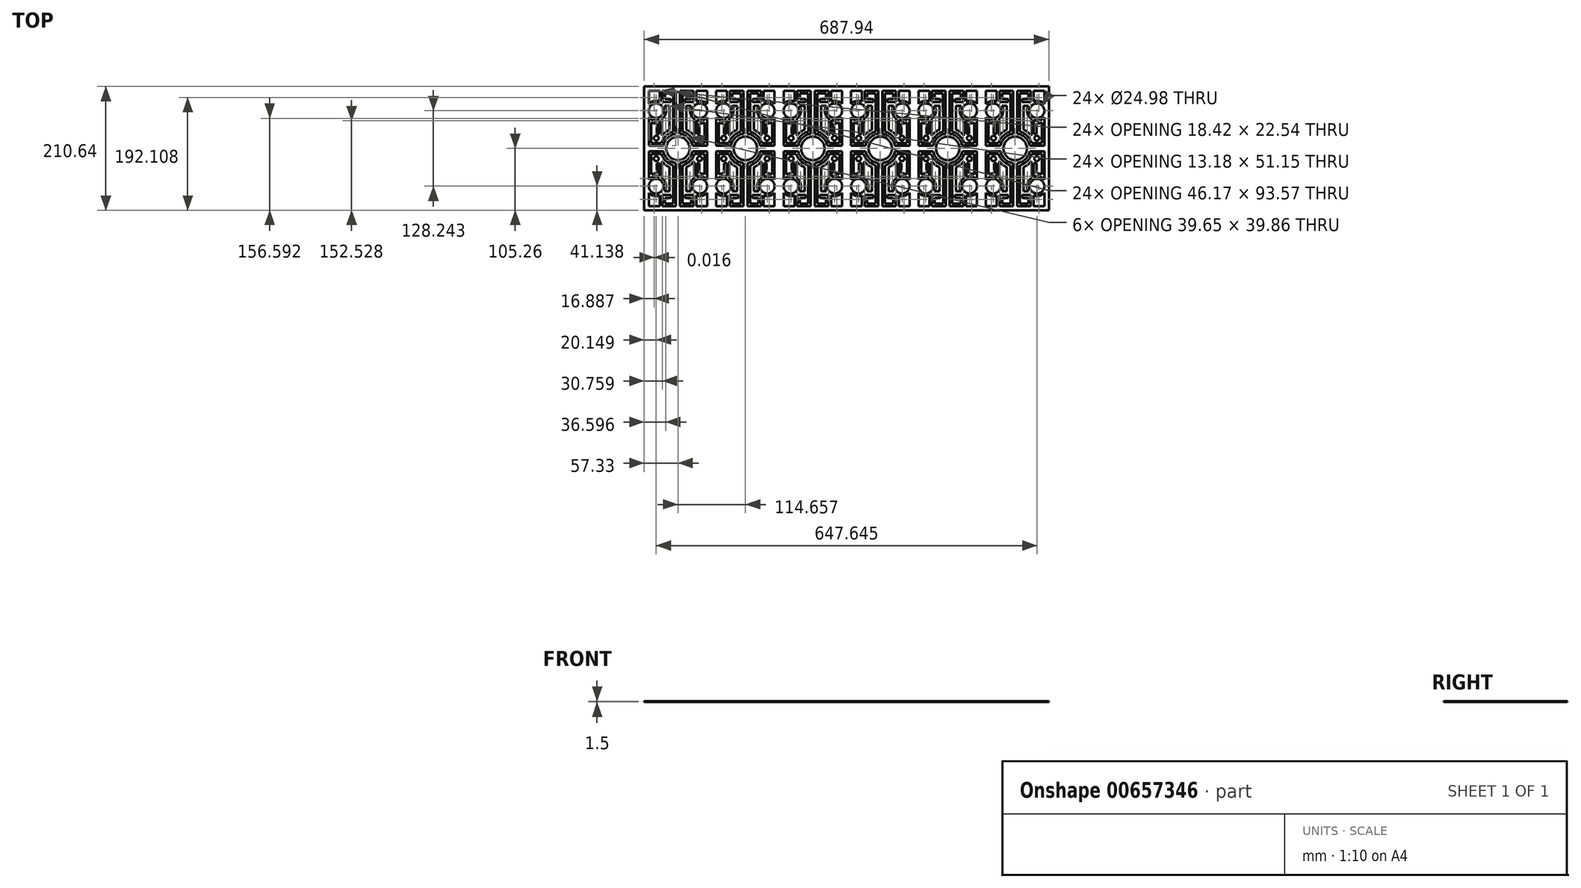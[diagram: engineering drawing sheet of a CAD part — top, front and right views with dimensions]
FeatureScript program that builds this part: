
annotation { "Feature Type Name" : "Feature", "Feature Type Description" : "" }
export const myFeature = defineFeature(function(context is Context, id is Id, definition is map)
    precondition{}
    {
        {
            var Q0;
            Q0=qCreatedBy(makeId("Top.planeOp"),FACE);
            var sketch = newSketch(context, id + "F0", { "sketchPlane" : qUnion([Q0])});
            skLineSegment(sketch, "E0.right", {"start": v(-57.33, -105.32) * mm, "end": v(-57.33, 105.32) * mm});
            skPoint(sketch, "E1.MirrorP", {"position": v(-114.66, 0) * mm});
            skLineSegment(sketch, "E2.MirrorCS", {"start": v(-137.32, -72.9) * mm, "end": v(-128.78, -72.9) * mm});
            skLineSegment(sketch, "E3.MirrorCS", {"start": v(-141.1, -98.18) * mm, "end": v(-141.1, -79.06) * mm});
            skLineSegment(sketch, "E4.MirrorCS", {"start": v(-136.9, 84.17) * mm, "end": v(-136.9, 93.38) * mm});
            skLineSegment(sketch, "E5.MirrorCS", {"start": v(-88.2, 98.06) * mm, "end": v(-88.2, 78.94) * mm});
            skLineSegment(sketch, "E6.MirrorCS", {"start": v(-83.03, 24.9) * mm, "end": v(-78.45, 24.9) * mm});
            skLineSegment(sketch, "E7.MirrorCS", {"start": v(-126.45, -79.06) * mm, "end": v(-126.45, -84.3) * mm});
            skLineSegment(sketch, "E8.MirrorCS", {"start": v(-136.89, -84.3) * mm, "end": v(-136.89, -93.5) * mm});
            skLineSegment(sketch, "E9.MirrorCS", {"start": v(-92.41, 84.17) * mm, "end": v(-92.41, 93.38) * mm});
            skLineSegment(sketch, "E10.MirrorCS", {"start": v(-141.1, 98.06) * mm, "end": v(-141.1, 78.94) * mm});
            skLineSegment(sketch, "E11.MirrorCS", {"start": v(-92.43, -84.3) * mm, "end": v(-92.43, -93.5) * mm});
            skLineSegment(sketch, "E12.MirrorCS", {"start": v(-83.04, -25.02) * mm, "end": v(-78.47, -25.02) * mm});
            skLineSegment(sketch, "E13.MirrorCS", {"start": v(-126.47, 78.94) * mm, "end": v(-126.47, 84.17) * mm});
            skLineSegment(sketch, "E14.MirrorCS", {"start": v(-146.29, 24.9) * mm, "end": v(-150.86, 24.9) * mm});
            skLineSegment(sketch, "E15.MirrorCS", {"start": v(-137.34, 72.78) * mm, "end": v(-128.8, 72.78) * mm});
            skLineSegment(sketch, "E16.MirrorCS", {"start": v(-92, -72.9) * mm, "end": v(-100.53, -72.9) * mm});
            skLineSegment(sketch, "E17.MirrorCS", {"start": v(-102.86, -79.06) * mm, "end": v(-102.86, -84.3) * mm});
            skArc(sketch, "E18.MirrorCS", {"start": v(-150.85, -42.56) * mm, "mid": v(-155.51, -42.86) * mm, "end": v(-160, -44.15) * mm});
            skArc(sketch, "E19.MirrorCS", {"start": v(-78.47, -42.56) * mm, "mid": v(-73.8, -42.86) * mm, "end": v(-69.3, -44.15) * mm});
            skArc(sketch, "E20.MirrorCS", {"start": v(-150.86, 42.44) * mm, "mid": v(-155.53, 42.74) * mm, "end": v(-160.03, 44.03) * mm});
            skArc(sketch, "E21.MirrorCS", {"start": v(-78.45, 42.44) * mm, "mid": v(-73.78, 42.74) * mm, "end": v(-69.29, 44.03) * mm});
            skLineSegment(sketch, "E22.MirrorCS", {"start": v(-91.98, 72.78) * mm, "end": v(-100.51, 72.78) * mm});
            skLineSegment(sketch, "E23.MirrorCS", {"start": v(-88.22, -98.18) * mm, "end": v(-88.22, -79.06) * mm});
            skLineSegment(sketch, "E24.MirrorCS", {"start": v(-146.27, -25.02) * mm, "end": v(-150.85, -25.02) * mm});
            skLineSegment(sketch, "E25.MirrorCS", {"start": v(-102.84, 78.94) * mm, "end": v(-102.84, 84.17) * mm});
            skCircle(sketch, "E26.MirrorC", {"center": v(-114.66, 0) * mm, "radius": 19.87 * mm});
            skPoint(sketch, "E27.MirrorP", {"position": v(-114.64, -0.12) * mm});
            skCircle(sketch, "E28.MirrorC", {"center": v(-114.64, -0.12) * mm, "radius": 19.87 * mm});
            skCircle(sketch, "E29.MirrorC", {"center": v(-151.48, -17.57) * mm, "radius": 4.15 * mm});
            skLineSegment(sketch, "E30.MirrorCS", {"start": v(-92.43, -93.5) * mm, "end": v(-106.74, -93.5) * mm});
            skLineSegment(sketch, "E31.MirrorCS", {"start": v(-102.86, -84.3) * mm, "end": v(-92.43, -84.3) * mm});
            skLineSegment(sketch, "E32.MirrorCS", {"start": v(-106.72, 93.38) * mm, "end": v(-106.82, 28.61) * mm});
            skLineSegment(sketch, "E33.MirrorCS", {"start": v(-164.31, 4.49) * mm, "end": v(-139.42, 4.49) * mm});
            skLineSegment(sketch, "E34.MirrorCS", {"start": v(-118.14, 98.06) * mm, "end": v(-141.1, 98.06) * mm});
            skLineSegment(sketch, "E35.MirrorCS", {"start": v(-118.13, -25.04) * mm, "end": v(-118.13, -98.18) * mm});
            skLineSegment(sketch, "E36.MirrorCS", {"start": v(-65, 4.49) * mm, "end": v(-89.9, 4.49) * mm});
            skLineSegment(sketch, "E37.MirrorCS", {"start": v(-164.3, -98.18) * mm, "end": v(-145.87, -98.18) * mm});
            skLineSegment(sketch, "E38.MirrorCS", {"start": v(-171.99, 105.32) * mm, "end": v(-57.33, 105.32) * mm});
            skLineSegment(sketch, "E39.MirrorCS", {"start": v(-83.44, -98.18) * mm, "end": v(-83.44, -80.04) * mm});
            skLineSegment(sketch, "E40.MirrorCS", {"start": v(-69.29, 9) * mm, "end": v(-86.39, 9) * mm});
            skLineSegment(sketch, "E41.MirrorCS", {"start": v(-100.53, -72.9) * mm, "end": v(-100.53, -31.97) * mm});
            skLineSegment(sketch, "E42.MirrorCS", {"start": v(-164.31, 98.06) * mm, "end": v(-145.89, 98.06) * mm});
            skArc(sketch, "E43.MirrorCS", {"start": v(-87.33, 21.63) * mm, "mid": v(-93.3, 27.54) * mm, "end": v(-100.51, 31.85) * mm});
            skLineSegment(sketch, "E44.MirrorCS", {"start": v(-128.8, 72.78) * mm, "end": v(-128.8, 31.85) * mm});
            skArc(sketch, "E45.MirrorCS", {"start": v(-141.97, -50.43) * mm, "mid": v(-135.25, -60.76) * mm, "end": v(-137.32, -72.9) * mm});
            skArc(sketch, "E46.MirrorCS", {"start": v(-65.02, -52.91) * mm, "mid": v(-73.34, -47.9) * mm, "end": v(-83.04, -48.31) * mm});
            skArc(sketch, "E47.MirrorCS", {"start": v(-65.02, -75.64) * mm, "mid": v(-73.56, -80.65) * mm, "end": v(-83.44, -80.04) * mm});
            skLineSegment(sketch, "E48.MirrorCS", {"start": v(-111.18, -25.04) * mm, "end": v(-111.18, -98.18) * mm});
            skCircle(sketch, "E49.MirrorC", {"center": v(-77.82, 17.45) * mm, "radius": 4.15 * mm});
            skLineSegment(sketch, "E50.MirrorCS", {"start": v(-145.89, 98.06) * mm, "end": v(-145.89, 79.92) * mm});
            skLineSegment(sketch, "E51.MirrorCS", {"start": v(-78.47, -25.02) * mm, "end": v(-78.47, -42.56) * mm});
            skLineSegment(sketch, "E52.MirrorCS", {"start": v(-136.89, -93.5) * mm, "end": v(-122.58, -93.5) * mm});
            skLineSegment(sketch, "E53.MirrorCS", {"start": v(-160, -44.15) * mm, "end": v(-160, -9.11) * mm});
            skArc(sketch, "E54.MirrorCS", {"start": v(-142.91, -9.11) * mm, "mid": v(-135.19, -21.52) * mm, "end": v(-122.47, -28.73) * mm});
            skLineSegment(sketch, "E55.MirrorCS", {"start": v(-150.85, -25.02) * mm, "end": v(-150.85, -42.56) * mm});
            skLineSegment(sketch, "E56.MirrorCS", {"start": v(-136.9, 93.38) * mm, "end": v(-122.6, 93.38) * mm});
            skLineSegment(sketch, "E57.MirrorCS", {"start": v(-102.84, 84.17) * mm, "end": v(-92.41, 84.17) * mm});
            skLineSegment(sketch, "E58.MirrorCS", {"start": v(-150.86, 24.9) * mm, "end": v(-150.86, 42.44) * mm});
            skCircle(sketch, "E59.MirrorC", {"center": v(-77.83, -17.57) * mm, "radius": 4.15 * mm});
            skLineSegment(sketch, "E60.MirrorCS", {"start": v(-100.51, 72.78) * mm, "end": v(-100.51, 31.85) * mm});
            skLineSegment(sketch, "E61.MirrorCS", {"start": v(-111.18, -98.18) * mm, "end": v(-88.22, -98.18) * mm});
            skLineSegment(sketch, "E62.MirrorCS", {"start": v(-160, -9.11) * mm, "end": v(-142.91, -9.11) * mm});
            skArc(sketch, "E63.MirrorCS", {"start": v(-164.3, -75.64) * mm, "mid": v(-155.76, -80.65) * mm, "end": v(-145.87, -80.04) * mm});
            skLineSegment(sketch, "E64.MirrorCS", {"start": v(-171.99, -105.32) * mm, "end": v(-57.33, -105.32) * mm});
            skPoint(sketch, "E65.MirrorP", {"position": v(-114.67, -0.12) * mm});
            skArc(sketch, "E66.MirrorCS", {"start": v(-65, 52.8) * mm, "mid": v(-73.32, 47.77) * mm, "end": v(-83.03, 48.2) * mm});
            skArc(sketch, "E67.MirrorCS", {"start": v(-89.9, 4.49) * mm, "mid": v(-97.22, 18.15) * mm, "end": v(-111.17, 24.92) * mm});
            skArc(sketch, "E68.MirrorCS", {"start": v(-87.35, -21.75) * mm, "mid": v(-93.32, -27.66) * mm, "end": v(-100.53, -31.97) * mm});
            skArc(sketch, "E69.MirrorCS", {"start": v(-86.4, -9.11) * mm, "mid": v(-94.13, -21.52) * mm, "end": v(-106.84, -28.73) * mm});
            skLineSegment(sketch, "E70.MirrorCS", {"start": v(-65.02, -98.18) * mm, "end": v(-65.02, -75.64) * mm});
            skLineSegment(sketch, "E71.MirrorCS", {"start": v(-164.3, -52.91) * mm, "end": v(-164.3, -4.6) * mm});
            skLineSegment(sketch, "E72.MirrorCS", {"start": v(-122.58, -93.5) * mm, "end": v(-122.47, -28.73) * mm});
            skLineSegment(sketch, "E73.MirrorCS", {"start": v(-69.3, -9.11) * mm, "end": v(-86.4, -9.11) * mm});
            skArc(sketch, "E74.MirrorCS", {"start": v(-164.31, 75.52) * mm, "mid": v(-155.77, 80.53) * mm, "end": v(-145.89, 79.92) * mm});
            skLineSegment(sketch, "E75.MirrorCS", {"start": v(-87.35, -50.43) * mm, "end": v(-87.35, -21.75) * mm});
            skLineSegment(sketch, "E76.MirrorCS", {"start": v(-141.1, 78.94) * mm, "end": v(-126.47, 78.94) * mm});
            skLineSegment(sketch, "E77.MirrorCS", {"start": v(-164.3, -98.18) * mm, "end": v(-164.3, -75.64) * mm});
            skLineSegment(sketch, "E78.MirrorCS", {"start": v(-65.02, -98.18) * mm, "end": v(-83.44, -98.18) * mm});
            skLineSegment(sketch, "E79.MirrorCS", {"start": v(-69.3, -44.15) * mm, "end": v(-69.3, -9.11) * mm});
            skLineSegment(sketch, "E80.MirrorCS", {"start": v(-146.27, -48.31) * mm, "end": v(-146.27, -25.02) * mm});
            skLineSegment(sketch, "E81.MirrorCS", {"start": v(-160.03, 9) * mm, "end": v(-142.93, 9) * mm});
            skLineSegment(sketch, "E82.MirrorCS", {"start": v(-141.97, -50.43) * mm, "end": v(-141.97, -21.75) * mm});
            skArc(sketch, "E83.MirrorCS", {"start": v(-87.33, 50.3) * mm, "mid": v(-94.05, 60.64) * mm, "end": v(-91.98, 72.78) * mm});
            skLineSegment(sketch, "E84.MirrorCS", {"start": v(-65.02, -52.91) * mm, "end": v(-65.02, -4.6) * mm});
            skLineSegment(sketch, "E85.MirrorCS", {"start": v(-164.31, 52.8) * mm, "end": v(-164.31, 4.49) * mm});
            skLineSegment(sketch, "E86.MirrorCS", {"start": v(-65, 98.06) * mm, "end": v(-83.43, 98.06) * mm});
            skCircle(sketch, "E87.MirrorC", {"center": v(-77.48, 64.06) * mm, "radius": 12.5 * mm});
            skLineSegment(sketch, "E88.MirrorCS", {"start": v(-78.45, 24.9) * mm, "end": v(-78.45, 42.44) * mm});
            skLineSegment(sketch, "E89.MirrorCS", {"start": v(-83.03, 48.2) * mm, "end": v(-83.03, 24.9) * mm});
            skLineSegment(sketch, "E90.MirrorCS", {"start": v(-171.99, -105.32) * mm, "end": v(-171.99, 105.32) * mm});
            skArc(sketch, "E91.MirrorCS", {"start": v(-65, 75.52) * mm, "mid": v(-73.54, 80.53) * mm, "end": v(-83.43, 79.92) * mm});
            skLineSegment(sketch, "E92.MirrorCS", {"start": v(-65, 52.8) * mm, "end": v(-65, 4.49) * mm});
            skArc(sketch, "E93.MirrorCS", {"start": v(-139.4, -4.6) * mm, "mid": v(-132.07, -18.27) * mm, "end": v(-118.13, -25.04) * mm});
            skLineSegment(sketch, "E94.MirrorCS", {"start": v(-83.04, -48.31) * mm, "end": v(-83.04, -25.02) * mm});
            skLineSegment(sketch, "E95.MirrorCS", {"start": v(-164.3, -4.6) * mm, "end": v(-139.4, -4.6) * mm});
            skLineSegment(sketch, "E96.MirrorCS", {"start": v(-88.2, 78.94) * mm, "end": v(-102.84, 78.94) * mm});
            skCircle(sketch, "E97.MirrorC", {"center": v(-151.5, 17.45) * mm, "radius": 4.15 * mm});
            skArc(sketch, "E98.MirrorCS", {"start": v(-141.97, -21.75) * mm, "mid": v(-136, -27.66) * mm, "end": v(-128.78, -31.97) * mm});
            skLineSegment(sketch, "E99.MirrorCS", {"start": v(-69.29, 44.03) * mm, "end": v(-69.29, 9) * mm});
            skArc(sketch, "E100.MirrorCS", {"start": v(-139.42, 4.49) * mm, "mid": v(-132.1, 18.15) * mm, "end": v(-118.14, 24.92) * mm});
            skLineSegment(sketch, "E101.MirrorCS", {"start": v(-88.22, -79.06) * mm, "end": v(-102.86, -79.06) * mm});
            skLineSegment(sketch, "E102.MirrorCS", {"start": v(-164.31, 98.06) * mm, "end": v(-164.31, 75.52) * mm});
            skArc(sketch, "E103.MirrorCS", {"start": v(-164.31, 52.8) * mm, "mid": v(-156, 47.77) * mm, "end": v(-146.29, 48.2) * mm});
            skCircle(sketch, "E104.MirrorC", {"center": v(-77.5, -64.18) * mm, "radius": 12.5 * mm});
            skLineSegment(sketch, "E105.MirrorCS", {"start": v(-111.17, 24.92) * mm, "end": v(-111.17, 98.06) * mm});
            skLineSegment(sketch, "E106.MirrorCS", {"start": v(-118.14, 24.92) * mm, "end": v(-118.14, 98.06) * mm});
            skCircle(sketch, "E107.MirrorC", {"center": v(-151.84, 64.06) * mm, "radius": 12.5 * mm});
            skArc(sketch, "E108.MirrorCS", {"start": v(-141.98, 21.63) * mm, "mid": v(-136.01, 27.54) * mm, "end": v(-128.8, 31.85) * mm});
            skLineSegment(sketch, "E109.MirrorCS", {"start": v(-160.03, 44.03) * mm, "end": v(-160.03, 9) * mm});
            skLineSegment(sketch, "E110.MirrorCS", {"start": v(-92.41, 93.38) * mm, "end": v(-106.72, 93.38) * mm});
            skLineSegment(sketch, "E111.MirrorCS", {"start": v(-141.1, -79.06) * mm, "end": v(-126.45, -79.06) * mm});
            skLineSegment(sketch, "E112.MirrorCS", {"start": v(-87.33, 50.3) * mm, "end": v(-87.33, 21.63) * mm});
            skLineSegment(sketch, "E113.MirrorCS", {"start": v(-146.29, 48.2) * mm, "end": v(-146.29, 24.9) * mm});
            skArc(sketch, "E114.MirrorCS", {"start": v(-87.35, -50.43) * mm, "mid": v(-94.06, -60.76) * mm, "end": v(-92, -72.9) * mm});
            skArc(sketch, "E115.MirrorCS", {"start": v(-164.3, -52.91) * mm, "mid": v(-155.98, -47.9) * mm, "end": v(-146.27, -48.31) * mm});
            skLineSegment(sketch, "E116.MirrorCS", {"start": v(-126.45, -84.3) * mm, "end": v(-136.89, -84.3) * mm});
            skArc(sketch, "E117.MirrorCS", {"start": v(-141.98, 50.3) * mm, "mid": v(-135.27, 60.64) * mm, "end": v(-137.34, 72.78) * mm});
            skLineSegment(sketch, "E118.MirrorCS", {"start": v(-65, 98.06) * mm, "end": v(-65, 75.52) * mm});
            skLineSegment(sketch, "E119.MirrorCS", {"start": v(-122.6, 93.38) * mm, "end": v(-122.5, 28.61) * mm});
            skLineSegment(sketch, "E120.MirrorCS", {"start": v(-106.74, -93.5) * mm, "end": v(-106.84, -28.73) * mm});
            skLineSegment(sketch, "E121.MirrorCS", {"start": v(-65.02, -4.6) * mm, "end": v(-89.91, -4.6) * mm});
            skLineSegment(sketch, "E122.MirrorCS", {"start": v(-83.43, 98.06) * mm, "end": v(-83.43, 79.92) * mm});
            skLineSegment(sketch, "E123.MirrorCS", {"start": v(-126.47, 84.17) * mm, "end": v(-136.9, 84.17) * mm});
            skLineSegment(sketch, "E124.MirrorCS", {"start": v(-111.17, 98.06) * mm, "end": v(-88.2, 98.06) * mm});
            skCircle(sketch, "E125.MirrorC", {"center": v(-151.82, -64.18) * mm, "radius": 12.5 * mm});
            skArc(sketch, "E126.MirrorCS", {"start": v(-142.93, 9) * mm, "mid": v(-135.2, 21.4) * mm, "end": v(-122.5, 28.61) * mm});
            skLineSegment(sketch, "E127.MirrorCS", {"start": v(-128.78, -72.9) * mm, "end": v(-128.78, -31.97) * mm});
            skLineSegment(sketch, "E128.MirrorCS", {"start": v(-118.13, -98.18) * mm, "end": v(-141.1, -98.18) * mm});
            skCircle(sketch, "E129.MirrorC", {"center": v(-114.67, -0.12) * mm, "radius": 19.87 * mm});
            skArc(sketch, "E130.MirrorCS", {"start": v(-89.91, -4.6) * mm, "mid": v(-97.24, -18.27) * mm, "end": v(-111.18, -25.04) * mm});
            skArc(sketch, "E131.MirrorCS", {"start": v(-86.39, 9) * mm, "mid": v(-94.11, 21.4) * mm, "end": v(-106.82, 28.61) * mm});
            skLineSegment(sketch, "E132.MirrorCS", {"start": v(-145.87, -98.18) * mm, "end": v(-145.87, -80.04) * mm});
            skLineSegment(sketch, "E133.MirrorCS", {"start": v(-141.98, 50.3) * mm, "end": v(-141.98, 21.63) * mm});
            skPoint(sketch, "E134.MirrorP", {"position": v(0, 0) * mm});
            skArc(sketch, "E135.MirrorCS", {"start": v(36.2, 42.44) * mm, "mid": v(40.87, 42.74) * mm, "end": v(45.37, 44.03) * mm});
            skLineSegment(sketch, "E136.MirrorCS", {"start": v(22.66, -72.9) * mm, "end": v(14.13, -72.9) * mm});
            skLineSegment(sketch, "E137.MirrorCS", {"start": v(-22.66, -72.9) * mm, "end": v(-14.13, -72.9) * mm});
            skLineSegment(sketch, "E138.MirrorCS", {"start": v(22.68, 72.78) * mm, "end": v(14.14, 72.78) * mm});
            skLineSegment(sketch, "E139.MirrorCS", {"start": v(31.63, 24.9) * mm, "end": v(36.2, 24.9) * mm});
            skLineSegment(sketch, "E140.MirrorCS", {"start": v(-26.45, 78.94) * mm, "end": v(-11.81, 78.94) * mm});
            skLineSegment(sketch, "E141.MirrorCS", {"start": v(26.44, -79.06) * mm, "end": v(11.8, -79.06) * mm});
            skLineSegment(sketch, "E142.MirrorCS", {"start": v(-11.8, -84.3) * mm, "end": v(-22.23, -84.3) * mm});
            skLineSegment(sketch, "E143.MirrorCS", {"start": v(-11.81, 84.17) * mm, "end": v(-22.25, 84.17) * mm});
            skLineSegment(sketch, "E144.MirrorCS", {"start": v(31.62, -25.02) * mm, "end": v(36.19, -25.02) * mm});
            skLineSegment(sketch, "E145.MirrorCS", {"start": v(26.44, -98.18) * mm, "end": v(26.44, -79.06) * mm});
            skLineSegment(sketch, "E146.MirrorCS", {"start": v(22.25, 84.17) * mm, "end": v(22.25, 93.38) * mm});
            skLineSegment(sketch, "E147.MirrorCS", {"start": v(-26.45, 98.06) * mm, "end": v(-26.45, 78.94) * mm});
            skLineSegment(sketch, "E148.MirrorCS", {"start": v(-26.44, -98.18) * mm, "end": v(-26.44, -79.06) * mm});
            skLineSegment(sketch, "E149.MirrorCS", {"start": v(11.81, 84.17) * mm, "end": v(22.25, 84.17) * mm});
            skLineSegment(sketch, "E150.MirrorCS", {"start": v(-31.63, 24.9) * mm, "end": v(-36.2, 24.9) * mm});
            skLineSegment(sketch, "E151.MirrorCS", {"start": v(-26.44, -79.06) * mm, "end": v(-11.8, -79.06) * mm});
            skLineSegment(sketch, "E152.MirrorCS", {"start": v(11.8, -84.3) * mm, "end": v(22.23, -84.3) * mm});
            skArc(sketch, "E153.MirrorCS", {"start": v(-36.2, 42.44) * mm, "mid": v(-40.87, 42.74) * mm, "end": v(-45.37, 44.03) * mm});
            skLineSegment(sketch, "E154.MirrorCS", {"start": v(11.8, -79.06) * mm, "end": v(11.8, -84.3) * mm});
            skLineSegment(sketch, "E155.MirrorCS", {"start": v(22.23, -84.3) * mm, "end": v(22.23, -93.5) * mm});
            skLineSegment(sketch, "E156.MirrorCS", {"start": v(-22.25, 84.17) * mm, "end": v(-22.25, 93.38) * mm});
            skLineSegment(sketch, "E157.MirrorCS", {"start": v(26.45, 98.06) * mm, "end": v(26.45, 78.94) * mm});
            skLineSegment(sketch, "E158.MirrorCS", {"start": v(-22.23, -84.3) * mm, "end": v(-22.23, -93.5) * mm});
            skLineSegment(sketch, "E159.MirrorCS", {"start": v(-31.62, -25.02) * mm, "end": v(-36.19, -25.02) * mm});
            skArc(sketch, "E160.MirrorCS", {"start": v(49.65, 52.8) * mm, "mid": v(41.34, 47.77) * mm, "end": v(31.63, 48.2) * mm});
            skArc(sketch, "E161.MirrorCS", {"start": v(36.19, -42.56) * mm, "mid": v(40.86, -42.86) * mm, "end": v(45.35, -44.15) * mm});
            skLineSegment(sketch, "E162.MirrorCS", {"start": v(26.45, 78.94) * mm, "end": v(11.81, 78.94) * mm});
            skLineSegment(sketch, "E163.MirrorCS", {"start": v(-11.8, -79.06) * mm, "end": v(-11.8, -84.3) * mm});
            skLineSegment(sketch, "E164.MirrorCS", {"start": v(-22.68, 72.78) * mm, "end": v(-14.14, 72.78) * mm});
            skArc(sketch, "E165.MirrorCS", {"start": v(-27.33, 21.63) * mm, "mid": v(-21.35, 27.54) * mm, "end": v(-14.14, 31.85) * mm});
            skArc(sketch, "E166.MirrorCS", {"start": v(-36.19, -42.56) * mm, "mid": v(-40.86, -42.86) * mm, "end": v(-45.35, -44.15) * mm});
            skLineSegment(sketch, "E167.MirrorCS", {"start": v(11.81, 78.94) * mm, "end": v(11.81, 84.17) * mm});
            skLineSegment(sketch, "E168.MirrorCS", {"start": v(-11.81, 78.94) * mm, "end": v(-11.81, 84.17) * mm});
            skCircle(sketch, "E169.MirrorC", {"center": v(0, 0) * mm, "radius": 19.87 * mm});
            skCircle(sketch, "E170.MirrorC", {"center": v(36.84, 17.45) * mm, "radius": 4.15 * mm});
            skCircle(sketch, "E171.MirrorC", {"center": v(-0.02, -0.12) * mm, "radius": 19.87 * mm});
            skCircle(sketch, "E172.MirrorC", {"center": v(-36.83, -17.57) * mm, "radius": 4.15 * mm});
            skPoint(sketch, "E173.MirrorP", {"position": v(0.02, -0.12) * mm});
            skCircle(sketch, "E174.MirrorC", {"center": v(-36.84, 17.45) * mm, "radius": 4.15 * mm});
            skCircle(sketch, "E175.MirrorC", {"center": v(36.83, -17.57) * mm, "radius": 4.15 * mm});
            skLineSegment(sketch, "E176.MirrorCS", {"start": v(49.64, -98.18) * mm, "end": v(49.64, -75.64) * mm});
            skLineSegment(sketch, "E177.MirrorCS", {"start": v(45.37, 9) * mm, "end": v(28.27, 9) * mm});
            skLineSegment(sketch, "E178.MirrorCS", {"start": v(-49.65, 98.06) * mm, "end": v(-31.23, 98.06) * mm});
            skLineSegment(sketch, "E179.MirrorCS", {"start": v(-49.64, -98.18) * mm, "end": v(-49.64, -75.64) * mm});
            skLineSegment(sketch, "E180.MirrorCS", {"start": v(45.35, -44.15) * mm, "end": v(45.35, -9.11) * mm});
            skLineSegment(sketch, "E181.MirrorCS", {"start": v(49.64, -98.18) * mm, "end": v(31.21, -98.18) * mm});
            skLineSegment(sketch, "E182.MirrorCS", {"start": v(27.33, 50.3) * mm, "end": v(27.33, 21.63) * mm});
            skArc(sketch, "E183.MirrorCS", {"start": v(27.33, 50.3) * mm, "mid": v(20.61, 60.64) * mm, "end": v(22.68, 72.78) * mm});
            skLineSegment(sketch, "E184.MirrorCS", {"start": v(49.65, 98.06) * mm, "end": v(49.65, 75.52) * mm});
            skLineSegment(sketch, "E185.MirrorCS", {"start": v(57.33, -105.32) * mm, "end": v(-57.33, -105.32) * mm});
            skLineSegment(sketch, "E186.MirrorCS", {"start": v(14.13, -72.9) * mm, "end": v(14.13, -31.97) * mm});
            skArc(sketch, "E187.MirrorCS", {"start": v(49.64, -75.64) * mm, "mid": v(41.1, -80.65) * mm, "end": v(31.21, -80.04) * mm});
            skArc(sketch, "E188.MirrorCS", {"start": v(-49.64, -75.64) * mm, "mid": v(-41.1, -80.65) * mm, "end": v(-31.21, -80.04) * mm});
            skLineSegment(sketch, "E189.MirrorCS", {"start": v(3.49, 24.92) * mm, "end": v(3.49, 98.06) * mm});
            skLineSegment(sketch, "E190.MirrorCS", {"start": v(-14.13, -72.9) * mm, "end": v(-14.13, -31.97) * mm});
            skLineSegment(sketch, "E191.MirrorCS", {"start": v(-49.64, -4.6) * mm, "end": v(-24.75, -4.6) * mm});
            skLineSegment(sketch, "E192.MirrorCS", {"start": v(-3.49, 24.92) * mm, "end": v(-3.49, 98.06) * mm});
            skLineSegment(sketch, "E193.MirrorCS", {"start": v(-7.92, -93.5) * mm, "end": v(-7.82, -28.73) * mm});
            skLineSegment(sketch, "E194.MirrorCS", {"start": v(-45.37, 9) * mm, "end": v(-28.27, 9) * mm});
            skLineSegment(sketch, "E195.MirrorCS", {"start": v(22.25, 93.38) * mm, "end": v(7.94, 93.38) * mm});
            skLineSegment(sketch, "E196.MirrorCS", {"start": v(-31.63, 48.2) * mm, "end": v(-31.63, 24.9) * mm});
            skLineSegment(sketch, "E197.MirrorCS", {"start": v(-45.35, -9.11) * mm, "end": v(-28.25, -9.11) * mm});
            skLineSegment(sketch, "E198.MirrorCS", {"start": v(57.33, -105.32) * mm, "end": v(57.33, 105.32) * mm});
            skArc(sketch, "E199.MirrorCS", {"start": v(49.65, 75.52) * mm, "mid": v(41.12, 80.53) * mm, "end": v(31.23, 79.92) * mm});
            skLineSegment(sketch, "E200.MirrorCS", {"start": v(-3.47, -25.04) * mm, "end": v(-3.47, -98.18) * mm});
            skLineSegment(sketch, "E201.MirrorCS", {"start": v(3.47, -98.18) * mm, "end": v(26.44, -98.18) * mm});
            skLineSegment(sketch, "E202.MirrorCS", {"start": v(-7.94, 93.38) * mm, "end": v(-7.83, 28.61) * mm});
            skLineSegment(sketch, "E203.MirrorCS", {"start": v(-27.33, 50.3) * mm, "end": v(-27.33, 21.63) * mm});
            skArc(sketch, "E204.MirrorCS", {"start": v(24.75, -4.6) * mm, "mid": v(17.42, -18.27) * mm, "end": v(3.47, -25.04) * mm});
            skLineSegment(sketch, "E205.MirrorCS", {"start": v(31.62, -48.31) * mm, "end": v(31.62, -25.02) * mm});
            skLineSegment(sketch, "E206.MirrorCS", {"start": v(31.21, -98.18) * mm, "end": v(31.21, -80.04) * mm});
            skLineSegment(sketch, "E207.MirrorCS", {"start": v(-45.35, -44.15) * mm, "end": v(-45.35, -9.11) * mm});
            skLineSegment(sketch, "E208.MirrorCS", {"start": v(49.64, -4.6) * mm, "end": v(24.75, -4.6) * mm});
            skLineSegment(sketch, "E209.MirrorCS", {"start": v(-22.25, 93.38) * mm, "end": v(-7.94, 93.38) * mm});
            skArc(sketch, "E210.MirrorCS", {"start": v(28.27, 9) * mm, "mid": v(20.55, 21.4) * mm, "end": v(7.83, 28.61) * mm});
            skCircle(sketch, "E211.MirrorC", {"center": v(-37.18, 64.06) * mm, "radius": 12.5 * mm});
            skLineSegment(sketch, "E212.MirrorCS", {"start": v(49.64, -52.91) * mm, "end": v(49.64, -4.6) * mm});
            skLineSegment(sketch, "E213.MirrorCS", {"start": v(57.33, 105.32) * mm, "end": v(-57.33, 105.32) * mm});
            skArc(sketch, "E214.MirrorCS", {"start": v(28.25, -9.11) * mm, "mid": v(20.53, -21.52) * mm, "end": v(7.82, -28.73) * mm});
            skLineSegment(sketch, "E215.MirrorCS", {"start": v(-49.65, 4.49) * mm, "end": v(-24.76, 4.49) * mm});
            skLineSegment(sketch, "E216.MirrorCS", {"start": v(22.23, -93.5) * mm, "end": v(7.92, -93.5) * mm});
            skLineSegment(sketch, "E217.MirrorCS", {"start": v(-22.23, -93.5) * mm, "end": v(-7.92, -93.5) * mm});
            skLineSegment(sketch, "E218.MirrorCS", {"start": v(-49.65, 98.06) * mm, "end": v(-49.65, 75.52) * mm});
            skLineSegment(sketch, "E219.MirrorCS", {"start": v(-49.65, 52.8) * mm, "end": v(-49.65, 4.49) * mm});
            skLineSegment(sketch, "E220.MirrorCS", {"start": v(-49.64, -52.91) * mm, "end": v(-49.64, -4.6) * mm});
            skArc(sketch, "E221.MirrorCS", {"start": v(-27.3, -21.75) * mm, "mid": v(-21.34, -27.66) * mm, "end": v(-14.13, -31.97) * mm});
            skArc(sketch, "E222.MirrorCS", {"start": v(27.33, 21.63) * mm, "mid": v(21.35, 27.54) * mm, "end": v(14.14, 31.85) * mm});
            skLineSegment(sketch, "E223.MirrorCS", {"start": v(-14.14, 72.78) * mm, "end": v(-14.14, 31.85) * mm});
            skLineSegment(sketch, "E224.MirrorCS", {"start": v(14.14, 72.78) * mm, "end": v(14.14, 31.85) * mm});
            skLineSegment(sketch, "E225.MirrorCS", {"start": v(-3.49, 98.06) * mm, "end": v(-26.45, 98.06) * mm});
            skLineSegment(sketch, "E226.MirrorCS", {"start": v(31.23, 98.06) * mm, "end": v(31.23, 79.92) * mm});
            skLineSegment(sketch, "E227.MirrorCS", {"start": v(3.49, 98.06) * mm, "end": v(26.45, 98.06) * mm});
            skArc(sketch, "E228.MirrorCS", {"start": v(-24.76, 4.49) * mm, "mid": v(-17.43, 18.15) * mm, "end": v(-3.49, 24.92) * mm});
            skArc(sketch, "E229.MirrorCS", {"start": v(-27.33, 50.3) * mm, "mid": v(-20.61, 60.64) * mm, "end": v(-22.68, 72.78) * mm});
            skLineSegment(sketch, "E230.MirrorCS", {"start": v(-36.19, -25.02) * mm, "end": v(-36.19, -42.56) * mm});
            skLineSegment(sketch, "E231.MirrorCS", {"start": v(3.47, -25.04) * mm, "end": v(3.47, -98.18) * mm});
            skArc(sketch, "E232.MirrorCS", {"start": v(-28.27, 9) * mm, "mid": v(-20.55, 21.4) * mm, "end": v(-7.83, 28.61) * mm});
            skArc(sketch, "E233.MirrorCS", {"start": v(49.64, -52.91) * mm, "mid": v(41.32, -47.9) * mm, "end": v(31.62, -48.31) * mm});
            skArc(sketch, "E234.MirrorCS", {"start": v(24.76, 4.49) * mm, "mid": v(17.43, 18.15) * mm, "end": v(3.49, 24.92) * mm});
            skLineSegment(sketch, "E235.MirrorCS", {"start": v(-45.37, 44.03) * mm, "end": v(-45.37, 9) * mm});
            skArc(sketch, "E236.MirrorCS", {"start": v(-27.3, -50.43) * mm, "mid": v(-20.6, -60.76) * mm, "end": v(-22.66, -72.9) * mm});
            skArc(sketch, "E237.MirrorCS", {"start": v(-24.75, -4.6) * mm, "mid": v(-17.42, -18.27) * mm, "end": v(-3.47, -25.04) * mm});
            skLineSegment(sketch, "E238.MirrorCS", {"start": v(-3.47, -98.18) * mm, "end": v(-26.44, -98.18) * mm});
            skArc(sketch, "E239.MirrorCS", {"start": v(27.3, -50.43) * mm, "mid": v(20.6, -60.76) * mm, "end": v(22.66, -72.9) * mm});
            skLineSegment(sketch, "E240.MirrorCS", {"start": v(31.63, 48.2) * mm, "end": v(31.63, 24.9) * mm});
            skLineSegment(sketch, "E241.MirrorCS", {"start": v(-36.2, 24.9) * mm, "end": v(-36.2, 42.44) * mm});
            skLineSegment(sketch, "E242.MirrorCS", {"start": v(36.19, -25.02) * mm, "end": v(36.19, -42.56) * mm});
            skLineSegment(sketch, "E243.MirrorCS", {"start": v(7.92, -93.5) * mm, "end": v(7.82, -28.73) * mm});
            skLineSegment(sketch, "E244.MirrorCS", {"start": v(-31.21, -98.18) * mm, "end": v(-31.21, -80.04) * mm});
            skCircle(sketch, "E245.MirrorC", {"center": v(-37.16, -64.18) * mm, "radius": 12.5 * mm});
            skLineSegment(sketch, "E246.MirrorCS", {"start": v(-27.3, -50.43) * mm, "end": v(-27.3, -21.75) * mm});
            skLineSegment(sketch, "E247.MirrorCS", {"start": v(45.37, 44.03) * mm, "end": v(45.37, 9) * mm});
            skCircle(sketch, "E248.MirrorC", {"center": v(37.18, 64.06) * mm, "radius": 12.5 * mm});
            skLineSegment(sketch, "E249.MirrorCS", {"start": v(7.94, 93.38) * mm, "end": v(7.83, 28.61) * mm});
            skLineSegment(sketch, "E250.MirrorCS", {"start": v(49.65, 4.49) * mm, "end": v(24.76, 4.49) * mm});
            skArc(sketch, "E251.MirrorCS", {"start": v(-49.64, -52.91) * mm, "mid": v(-41.32, -47.9) * mm, "end": v(-31.62, -48.31) * mm});
            skLineSegment(sketch, "E252.MirrorCS", {"start": v(36.2, 24.9) * mm, "end": v(36.2, 42.44) * mm});
            skArc(sketch, "E253.MirrorCS", {"start": v(27.3, -21.75) * mm, "mid": v(21.34, -27.66) * mm, "end": v(14.13, -31.97) * mm});
            skCircle(sketch, "E254.MirrorC", {"center": v(37.16, -64.18) * mm, "radius": 12.5 * mm});
            skLineSegment(sketch, "E255.MirrorCS", {"start": v(27.3, -50.43) * mm, "end": v(27.3, -21.75) * mm});
            skCircle(sketch, "E256.MirrorC", {"center": v(0.02, -0.12) * mm, "radius": 19.87 * mm});
            skLineSegment(sketch, "E257.MirrorCS", {"start": v(45.35, -9.11) * mm, "end": v(28.25, -9.11) * mm});
            skLineSegment(sketch, "E258.MirrorCS", {"start": v(49.65, 52.8) * mm, "end": v(49.65, 4.49) * mm});
            skLineSegment(sketch, "E259.MirrorCS", {"start": v(-49.64, -98.18) * mm, "end": v(-31.21, -98.18) * mm});
            skLineSegment(sketch, "E260.MirrorCS", {"start": v(-31.23, 98.06) * mm, "end": v(-31.23, 79.92) * mm});
            skLineSegment(sketch, "E261.MirrorCS", {"start": v(-31.62, -48.31) * mm, "end": v(-31.62, -25.02) * mm});
            skLineSegment(sketch, "E262.MirrorCS", {"start": v(49.65, 98.06) * mm, "end": v(31.23, 98.06) * mm});
            skArc(sketch, "E263.MirrorCS", {"start": v(-49.65, 75.52) * mm, "mid": v(-41.12, 80.53) * mm, "end": v(-31.23, 79.92) * mm});
            skArc(sketch, "E264.MirrorCS", {"start": v(-49.65, 52.8) * mm, "mid": v(-41.34, 47.77) * mm, "end": v(-31.63, 48.2) * mm});
            skArc(sketch, "E265.MirrorCS", {"start": v(-28.25, -9.11) * mm, "mid": v(-20.53, -21.52) * mm, "end": v(-7.82, -28.73) * mm});
            skPoint(sketch, "E266.MirrorP", {"position": v(229.31, 0) * mm});
            skPoint(sketch, "E267.MirrorP", {"position": v(114.66, 0) * mm});
            skLineSegment(sketch, "E268.MirrorCS", {"start": v(260.93, -25.02) * mm, "end": v(265.5, -25.02) * mm});
            skLineSegment(sketch, "E269.MirrorCS", {"start": v(197.68, 24.9) * mm, "end": v(193.1, 24.9) * mm});
            skArc(sketch, "E270.MirrorCS", {"start": v(265.52, 42.44) * mm, "mid": v(270.19, 42.74) * mm, "end": v(274.68, 44.03) * mm});
            skLineSegment(sketch, "E271.MirrorCS", {"start": v(137.34, 72.78) * mm, "end": v(128.8, 72.78) * mm});
            skLineSegment(sketch, "E272.MirrorCS", {"start": v(126.45, -84.3) * mm, "end": v(136.89, -84.3) * mm});
            skLineSegment(sketch, "E273.MirrorCS", {"start": v(102.84, 78.94) * mm, "end": v(102.84, 84.17) * mm});
            skLineSegment(sketch, "E274.MirrorCS", {"start": v(206.65, -72.9) * mm, "end": v(215.19, -72.9) * mm});
            skPoint(sketch, "E275.MirrorP", {"position": v(229.3, -0.12) * mm});
            skArc(sketch, "E276.MirrorCS", {"start": v(179.68, -52.91) * mm, "mid": v(188, -47.9) * mm, "end": v(197.7, -48.31) * mm});
            skArc(sketch, "E277.MirrorCS", {"start": v(193.1, 42.44) * mm, "mid": v(188.44, 42.74) * mm, "end": v(183.94, 44.03) * mm});
            skLineSegment(sketch, "E278.MirrorCS", {"start": v(126.47, 84.17) * mm, "end": v(136.9, 84.17) * mm});
            skLineSegment(sketch, "E279.MirrorCS", {"start": v(146.29, 24.9) * mm, "end": v(150.86, 24.9) * mm});
            skArc(sketch, "E280.MirrorCS", {"start": v(164.3, -52.91) * mm, "mid": v(155.98, -47.9) * mm, "end": v(146.27, -48.31) * mm});
            skLineSegment(sketch, "E281.MirrorCS", {"start": v(251.54, -84.3) * mm, "end": v(251.54, -93.5) * mm});
            skLineSegment(sketch, "E282.MirrorCS", {"start": v(92.43, -84.3) * mm, "end": v(92.43, -93.5) * mm});
            skLineSegment(sketch, "E283.MirrorCS", {"start": v(126.45, -79.06) * mm, "end": v(126.45, -84.3) * mm});
            skLineSegment(sketch, "E284.MirrorCS", {"start": v(88.22, -79.06) * mm, "end": v(102.86, -79.06) * mm});
            skLineSegment(sketch, "E285.MirrorCS", {"start": v(241.13, 84.17) * mm, "end": v(251.56, 84.17) * mm});
            skLineSegment(sketch, "E286.MirrorCS", {"start": v(88.2, 98.06) * mm, "end": v(88.2, 78.94) * mm});
            skLineSegment(sketch, "E287.MirrorCS", {"start": v(137.32, -72.9) * mm, "end": v(128.78, -72.9) * mm});
            skLineSegment(sketch, "E288.MirrorCS", {"start": v(202.88, -98.18) * mm, "end": v(202.88, -79.06) * mm});
            skLineSegment(sketch, "E289.MirrorCS", {"start": v(141.1, -79.06) * mm, "end": v(126.45, -79.06) * mm});
            skArc(sketch, "E290.MirrorCS", {"start": v(193.12, -42.56) * mm, "mid": v(188.46, -42.86) * mm, "end": v(183.96, -44.15) * mm});
            skLineSegment(sketch, "E291.MirrorCS", {"start": v(255.76, 78.94) * mm, "end": v(241.13, 78.94) * mm});
            skPoint(sketch, "E292.MirrorP", {"position": v(114.67, -0.12) * mm});
            skLineSegment(sketch, "E293.MirrorCS", {"start": v(260.94, 24.9) * mm, "end": v(265.52, 24.9) * mm});
            skLineSegment(sketch, "E294.MirrorCS", {"start": v(251.56, 84.17) * mm, "end": v(251.56, 93.38) * mm});
            skLineSegment(sketch, "E295.MirrorCS", {"start": v(102.86, -84.3) * mm, "end": v(92.43, -84.3) * mm});
            skLineSegment(sketch, "E296.MirrorCS", {"start": v(141.1, 78.94) * mm, "end": v(126.47, 78.94) * mm});
            skLineSegment(sketch, "E297.MirrorCS", {"start": v(91.98, 72.78) * mm, "end": v(100.51, 72.78) * mm});
            skArc(sketch, "E298.MirrorCS", {"start": v(278.95, -52.91) * mm, "mid": v(270.63, -47.9) * mm, "end": v(260.93, -48.31) * mm});
            skLineSegment(sketch, "E299.MirrorCS", {"start": v(83.04, -25.02) * mm, "end": v(78.47, -25.02) * mm});
            skLineSegment(sketch, "E300.MirrorCS", {"start": v(217.52, -84.3) * mm, "end": v(207.08, -84.3) * mm});
            skLineSegment(sketch, "E301.MirrorCS", {"start": v(202.86, 78.94) * mm, "end": v(217.5, 78.94) * mm});
            skLineSegment(sketch, "E302.MirrorCS", {"start": v(252, 72.78) * mm, "end": v(243.46, 72.78) * mm});
            skLineSegment(sketch, "E303.MirrorCS", {"start": v(217.5, 84.17) * mm, "end": v(207.07, 84.17) * mm});
            skLineSegment(sketch, "E304.MirrorCS", {"start": v(255.75, -98.18) * mm, "end": v(255.75, -79.06) * mm});
            skArc(sketch, "E305.MirrorCS", {"start": v(265.5, -42.56) * mm, "mid": v(270.17, -42.86) * mm, "end": v(274.67, -44.15) * mm});
            skLineSegment(sketch, "E306.MirrorCS", {"start": v(88.2, 78.94) * mm, "end": v(102.84, 78.94) * mm});
            skLineSegment(sketch, "E307.MirrorCS", {"start": v(88.22, -98.18) * mm, "end": v(88.22, -79.06) * mm});
            skLineSegment(sketch, "E308.MirrorCS", {"start": v(202.88, -79.06) * mm, "end": v(217.52, -79.06) * mm});
            skLineSegment(sketch, "E309.MirrorCS", {"start": v(102.86, -79.06) * mm, "end": v(102.86, -84.3) * mm});
            skArc(sketch, "E310.MirrorCS", {"start": v(164.31, 52.8) * mm, "mid": v(156, 47.77) * mm, "end": v(146.29, 48.2) * mm});
            skLineSegment(sketch, "E311.MirrorCS", {"start": v(202.86, 98.06) * mm, "end": v(202.86, 78.94) * mm});
            skLineSegment(sketch, "E312.MirrorCS", {"start": v(217.52, -79.06) * mm, "end": v(217.52, -84.3) * mm});
            skLineSegment(sketch, "E313.MirrorCS", {"start": v(92, -72.9) * mm, "end": v(100.53, -72.9) * mm});
            skLineSegment(sketch, "E314.MirrorCS", {"start": v(255.75, -79.06) * mm, "end": v(241.11, -79.06) * mm});
            skArc(sketch, "E315.MirrorCS", {"start": v(78.45, 42.44) * mm, "mid": v(73.78, 42.74) * mm, "end": v(69.29, 44.03) * mm});
            skArc(sketch, "E316.MirrorCS", {"start": v(78.47, -42.56) * mm, "mid": v(73.8, -42.86) * mm, "end": v(69.3, -44.15) * mm});
            skLineSegment(sketch, "E317.MirrorCS", {"start": v(207.08, -84.3) * mm, "end": v(207.08, -93.5) * mm});
            skArc(sketch, "E318.MirrorCS", {"start": v(65.02, -52.91) * mm, "mid": v(73.34, -47.9) * mm, "end": v(83.04, -48.31) * mm});
            skLineSegment(sketch, "E319.MirrorCS", {"start": v(126.47, 78.94) * mm, "end": v(126.47, 84.17) * mm});
            skLineSegment(sketch, "E320.MirrorCS", {"start": v(241.13, 78.94) * mm, "end": v(241.13, 84.17) * mm});
            skLineSegment(sketch, "E321.MirrorCS", {"start": v(251.98, -72.9) * mm, "end": v(243.44, -72.9) * mm});
            skLineSegment(sketch, "E322.MirrorCS", {"start": v(206.63, 72.78) * mm, "end": v(215.17, 72.78) * mm});
            skLineSegment(sketch, "E323.MirrorCS", {"start": v(241.11, -84.3) * mm, "end": v(251.54, -84.3) * mm});
            skLineSegment(sketch, "E324.MirrorCS", {"start": v(217.5, 78.94) * mm, "end": v(217.5, 84.17) * mm});
            skLineSegment(sketch, "E325.MirrorCS", {"start": v(92.41, 84.17) * mm, "end": v(92.41, 93.38) * mm});
            skLineSegment(sketch, "E326.MirrorCS", {"start": v(136.9, 84.17) * mm, "end": v(136.9, 93.38) * mm});
            skLineSegment(sketch, "E327.MirrorCS", {"start": v(102.84, 84.17) * mm, "end": v(92.41, 84.17) * mm});
            skLineSegment(sketch, "E328.MirrorCS", {"start": v(207.07, 84.17) * mm, "end": v(207.07, 93.38) * mm});
            skLineSegment(sketch, "E329.MirrorCS", {"start": v(136.89, -84.3) * mm, "end": v(136.89, -93.5) * mm});
            skLineSegment(sketch, "E330.MirrorCS", {"start": v(197.7, -25.02) * mm, "end": v(193.12, -25.02) * mm});
            skLineSegment(sketch, "E331.MirrorCS", {"start": v(255.76, 98.06) * mm, "end": v(255.76, 78.94) * mm});
            skArc(sketch, "E332.MirrorCS", {"start": v(150.85, -42.56) * mm, "mid": v(155.51, -42.86) * mm, "end": v(160, -44.15) * mm});
            skArc(sketch, "E333.MirrorCS", {"start": v(150.86, 42.44) * mm, "mid": v(155.53, 42.74) * mm, "end": v(160.03, 44.03) * mm});
            skLineSegment(sketch, "E334.MirrorCS", {"start": v(241.11, -79.06) * mm, "end": v(241.11, -84.3) * mm});
            skLineSegment(sketch, "E335.MirrorCS", {"start": v(146.27, -25.02) * mm, "end": v(150.85, -25.02) * mm});
            skLineSegment(sketch, "E336.MirrorCS", {"start": v(83.03, 24.9) * mm, "end": v(78.45, 24.9) * mm});
            skPoint(sketch, "E337.MirrorP", {"position": v(114.64, -0.12) * mm});
            skCircle(sketch, "E338.MirrorC", {"center": v(229.33, -0.12) * mm, "radius": 19.87 * mm});
            skCircle(sketch, "E339.MirrorC", {"center": v(77.82, 17.45) * mm, "radius": 4.15 * mm});
            skCircle(sketch, "E340.MirrorC", {"center": v(151.48, -17.57) * mm, "radius": 4.15 * mm});
            skCircle(sketch, "E341.MirrorC", {"center": v(77.83, -17.57) * mm, "radius": 4.15 * mm});
            skCircle(sketch, "E342.MirrorC", {"center": v(114.66, 0) * mm, "radius": 19.87 * mm});
            skCircle(sketch, "E343.MirrorC", {"center": v(229.31, 0) * mm, "radius": 19.87 * mm});
            skCircle(sketch, "E344.MirrorC", {"center": v(151.5, 17.45) * mm, "radius": 4.15 * mm});
            skCircle(sketch, "E345.MirrorC", {"center": v(192.49, -17.57) * mm, "radius": 4.15 * mm});
            skCircle(sketch, "E346.MirrorC", {"center": v(266.14, -17.57) * mm, "radius": 4.15 * mm});
            skCircle(sketch, "E347.MirrorC", {"center": v(192.47, 17.45) * mm, "radius": 4.15 * mm});
            skCircle(sketch, "E348.MirrorC", {"center": v(266.15, 17.45) * mm, "radius": 4.15 * mm});
            skCircle(sketch, "E349.MirrorC", {"center": v(114.64, -0.12) * mm, "radius": 19.87 * mm});
            skLineSegment(sketch, "E350.MirrorCS", {"start": v(83.03, 48.2) * mm, "end": v(83.03, 24.9) * mm});
            skLineSegment(sketch, "E351.MirrorCS", {"start": v(179.68, -4.6) * mm, "end": v(204.57, -4.6) * mm});
            skLineSegment(sketch, "E352.MirrorCS", {"start": v(128.8, 72.78) * mm, "end": v(128.8, 31.85) * mm});
            skLineSegment(sketch, "E353.MirrorCS", {"start": v(215.19, -72.9) * mm, "end": v(215.19, -31.97) * mm});
            skLineSegment(sketch, "E354.MirrorCS", {"start": v(197.68, 48.2) * mm, "end": v(197.68, 24.9) * mm});
            skCircle(sketch, "E355.MirrorC", {"center": v(151.84, 64.06) * mm, "radius": 12.5 * mm});
            skArc(sketch, "E356.MirrorCS", {"start": v(201.06, -9.11) * mm, "mid": v(208.78, -21.52) * mm, "end": v(221.5, -28.73) * mm});
            skArc(sketch, "E357.MirrorCS", {"start": v(89.91, -4.6) * mm, "mid": v(97.24, -18.27) * mm, "end": v(111.18, -25.04) * mm});
            skLineSegment(sketch, "E358.MirrorCS", {"start": v(256.62, -50.43) * mm, "end": v(256.62, -21.75) * mm});
            skArc(sketch, "E359.MirrorCS", {"start": v(179.66, 75.52) * mm, "mid": v(188.2, 80.53) * mm, "end": v(198.08, 79.92) * mm});
            skArc(sketch, "E360.MirrorCS", {"start": v(204.57, -4.6) * mm, "mid": v(211.9, -18.27) * mm, "end": v(225.84, -25.04) * mm});
            skLineSegment(sketch, "E361.MirrorCS", {"start": v(160, -9.11) * mm, "end": v(142.91, -9.11) * mm});
            skLineSegment(sketch, "E362.MirrorCS", {"start": v(65.02, -98.18) * mm, "end": v(83.44, -98.18) * mm});
            skArc(sketch, "E363.MirrorCS", {"start": v(202, -50.43) * mm, "mid": v(208.72, -60.76) * mm, "end": v(206.65, -72.9) * mm});
            skArc(sketch, "E364.MirrorCS", {"start": v(164.31, 75.52) * mm, "mid": v(155.77, 80.53) * mm, "end": v(145.89, 79.92) * mm});
            skLineSegment(sketch, "E365.MirrorCS", {"start": v(251.54, -93.5) * mm, "end": v(237.23, -93.5) * mm});
            skLineSegment(sketch, "E366.MirrorCS", {"start": v(215.17, 72.78) * mm, "end": v(215.17, 31.85) * mm});
            skLineSegment(sketch, "E367.MirrorCS", {"start": v(198.1, -98.18) * mm, "end": v(198.1, -80.04) * mm});
            skLineSegment(sketch, "E368.MirrorCS", {"start": v(260.94, 48.2) * mm, "end": v(260.94, 24.9) * mm});
            skCircle(sketch, "E369.MirrorC", {"center": v(77.5, -64.18) * mm, "radius": 12.5 * mm});
            skLineSegment(sketch, "E370.MirrorCS", {"start": v(111.17, 98.06) * mm, "end": v(88.2, 98.06) * mm});
            skLineSegment(sketch, "E371.MirrorCS", {"start": v(160, -44.15) * mm, "end": v(160, -9.11) * mm});
            skLineSegment(sketch, "E372.MirrorCS", {"start": v(65.02, -98.18) * mm, "end": v(65.02, -75.64) * mm});
            skLineSegment(sketch, "E373.MirrorCS", {"start": v(111.18, -25.04) * mm, "end": v(111.18, -98.18) * mm});
            skLineSegment(sketch, "E374.MirrorCS", {"start": v(274.68, 44.03) * mm, "end": v(274.68, 9) * mm});
            skLineSegment(sketch, "E375.MirrorCS", {"start": v(274.67, -9.11) * mm, "end": v(257.57, -9.11) * mm});
            skArc(sketch, "E376.MirrorCS", {"start": v(87.35, -50.43) * mm, "mid": v(94.06, -60.76) * mm, "end": v(92, -72.9) * mm});
            skLineSegment(sketch, "E377.MirrorCS", {"start": v(278.95, -98.18) * mm, "end": v(260.53, -98.18) * mm});
            skLineSegment(sketch, "E378.MirrorCS", {"start": v(65, 98.06) * mm, "end": v(65, 75.52) * mm});
            skLineSegment(sketch, "E379.MirrorCS", {"start": v(183.94, 44.03) * mm, "end": v(183.94, 9) * mm});
            skLineSegment(sketch, "E380.MirrorCS", {"start": v(160.03, 44.03) * mm, "end": v(160.03, 9) * mm});
            skLineSegment(sketch, "E381.MirrorCS", {"start": v(141.1, -98.18) * mm, "end": v(141.1, -79.06) * mm});
            skLineSegment(sketch, "E382.MirrorCS", {"start": v(106.72, 93.38) * mm, "end": v(106.82, 28.61) * mm});
            skLineSegment(sketch, "E383.MirrorCS", {"start": v(65.02, -52.91) * mm, "end": v(65.02, -4.6) * mm});
            skLineSegment(sketch, "E384.MirrorCS", {"start": v(146.29, 48.2) * mm, "end": v(146.29, 24.9) * mm});
            skArc(sketch, "E385.MirrorCS", {"start": v(256.64, 21.63) * mm, "mid": v(250.67, 27.54) * mm, "end": v(243.46, 31.85) * mm});
            skLineSegment(sketch, "E386.MirrorCS", {"start": v(198.08, 98.06) * mm, "end": v(198.08, 79.92) * mm});
            skLineSegment(sketch, "E387.MirrorCS", {"start": v(83.44, -98.18) * mm, "end": v(83.44, -80.04) * mm});
            skLineSegment(sketch, "E388.MirrorCS", {"start": v(69.3, -44.15) * mm, "end": v(69.3, -9.11) * mm});
            skLineSegment(sketch, "E389.MirrorCS", {"start": v(183.96, -44.15) * mm, "end": v(183.96, -9.11) * mm});
            skArc(sketch, "E390.MirrorCS", {"start": v(141.98, 50.3) * mm, "mid": v(135.27, 60.64) * mm, "end": v(137.34, 72.78) * mm});
            skCircle(sketch, "E391.MirrorC", {"center": v(151.82, -64.18) * mm, "radius": 12.5 * mm});
            skArc(sketch, "E392.MirrorCS", {"start": v(139.4, -4.6) * mm, "mid": v(132.07, -18.27) * mm, "end": v(118.13, -25.04) * mm});
            skLineSegment(sketch, "E393.MirrorCS", {"start": v(145.87, -98.18) * mm, "end": v(145.87, -80.04) * mm});
            skArc(sketch, "E394.MirrorCS", {"start": v(87.35, -21.75) * mm, "mid": v(93.32, -27.66) * mm, "end": v(100.53, -31.97) * mm});
            skLineSegment(sketch, "E395.MirrorCS", {"start": v(179.66, 52.8) * mm, "end": v(179.66, 4.49) * mm});
            skArc(sketch, "E396.MirrorCS", {"start": v(139.42, 4.49) * mm, "mid": v(132.1, 18.15) * mm, "end": v(118.14, 24.92) * mm});
            skLineSegment(sketch, "E397.MirrorCS", {"start": v(106.74, -93.5) * mm, "end": v(106.84, -28.73) * mm});
            skLineSegment(sketch, "E398.MirrorCS", {"start": v(286.64, -105.32) * mm, "end": v(286.64, 105.32) * mm});
            skLineSegment(sketch, "E399.MirrorCS", {"start": v(225.83, 24.92) * mm, "end": v(225.83, 98.06) * mm});
            skLineSegment(sketch, "E400.MirrorCS", {"start": v(243.46, 72.78) * mm, "end": v(243.46, 31.85) * mm});
            skLineSegment(sketch, "E401.MirrorCS", {"start": v(118.13, -25.04) * mm, "end": v(118.13, -98.18) * mm});
            skLineSegment(sketch, "E402.MirrorCS", {"start": v(92.43, -93.5) * mm, "end": v(106.74, -93.5) * mm});
            skLineSegment(sketch, "E403.MirrorCS", {"start": v(179.66, 98.06) * mm, "end": v(179.66, 75.52) * mm});
            skArc(sketch, "E404.MirrorCS", {"start": v(257.57, -9.11) * mm, "mid": v(249.84, -21.52) * mm, "end": v(237.13, -28.73) * mm});
            skLineSegment(sketch, "E405.MirrorCS", {"start": v(69.3, -9.11) * mm, "end": v(86.4, -9.11) * mm});
            skLineSegment(sketch, "E406.MirrorCS", {"start": v(150.86, 24.9) * mm, "end": v(150.86, 42.44) * mm});
            skLineSegment(sketch, "E407.MirrorCS", {"start": v(146.27, -48.31) * mm, "end": v(146.27, -25.02) * mm});
            skLineSegment(sketch, "E408.MirrorCS", {"start": v(78.45, 24.9) * mm, "end": v(78.45, 42.44) * mm});
            skArc(sketch, "E409.MirrorCS", {"start": v(164.3, -75.64) * mm, "mid": v(155.76, -80.65) * mm, "end": v(145.87, -80.04) * mm});
            skLineSegment(sketch, "E410.MirrorCS", {"start": v(251.56, 93.38) * mm, "end": v(237.25, 93.38) * mm});
            skLineSegment(sketch, "E411.MirrorCS", {"start": v(183.96, -9.11) * mm, "end": v(201.06, -9.11) * mm});
            skLineSegment(sketch, "E412.MirrorCS", {"start": v(237.23, -93.5) * mm, "end": v(237.13, -28.73) * mm});
            skCircle(sketch, "E413.MirrorC", {"center": v(266.48, -64.18) * mm, "radius": 12.5 * mm});
            skLineSegment(sketch, "E414.MirrorCS", {"start": v(145.89, 98.06) * mm, "end": v(145.89, 79.92) * mm});
            skLineSegment(sketch, "E415.MirrorCS", {"start": v(201.99, 50.3) * mm, "end": v(201.99, 21.63) * mm});
            skLineSegment(sketch, "E416.MirrorCS", {"start": v(164.3, -98.18) * mm, "end": v(145.87, -98.18) * mm});
            skLineSegment(sketch, "E417.MirrorCS", {"start": v(278.97, 98.06) * mm, "end": v(260.54, 98.06) * mm});
            skLineSegment(sketch, "E418.MirrorCS", {"start": v(141.98, 50.3) * mm, "end": v(141.98, 21.63) * mm});
            skLineSegment(sketch, "E419.MirrorCS", {"start": v(183.94, 9) * mm, "end": v(201.04, 9) * mm});
            skLineSegment(sketch, "E420.MirrorCS", {"start": v(164.3, -4.6) * mm, "end": v(139.4, -4.6) * mm});
            skLineSegment(sketch, "E421.MirrorCS", {"start": v(274.68, 9) * mm, "end": v(257.58, 9) * mm});
            skLineSegment(sketch, "E422.MirrorCS", {"start": v(221.4, -93.5) * mm, "end": v(221.5, -28.73) * mm});
            skLineSegment(sketch, "E423.MirrorCS", {"start": v(232.8, 24.92) * mm, "end": v(232.8, 98.06) * mm});
            skLineSegment(sketch, "E424.MirrorCS", {"start": v(237.25, 93.38) * mm, "end": v(237.15, 28.61) * mm});
            skLineSegment(sketch, "E425.MirrorCS", {"start": v(286.64, -105.32) * mm, "end": v(171.99, -105.32) * mm});
            skLineSegment(sketch, "E426.MirrorCS", {"start": v(225.83, 98.06) * mm, "end": v(202.86, 98.06) * mm});
            skArc(sketch, "E427.MirrorCS", {"start": v(256.62, -21.75) * mm, "mid": v(250.65, -27.66) * mm, "end": v(243.44, -31.97) * mm});
            skLineSegment(sketch, "E428.MirrorCS", {"start": v(278.97, 52.8) * mm, "end": v(278.97, 4.49) * mm});
            skLineSegment(sketch, "E429.MirrorCS", {"start": v(232.79, -25.04) * mm, "end": v(232.79, -98.18) * mm});
            skArc(sketch, "E430.MirrorCS", {"start": v(141.97, -21.75) * mm, "mid": v(136, -27.66) * mm, "end": v(128.78, -31.97) * mm});
            skLineSegment(sketch, "E431.MirrorCS", {"start": v(193.12, -25.02) * mm, "end": v(193.12, -42.56) * mm});
            skCircle(sketch, "E432.MirrorC", {"center": v(77.48, 64.06) * mm, "radius": 12.5 * mm});
            skArc(sketch, "E433.MirrorCS", {"start": v(254.08, 4.49) * mm, "mid": v(246.75, 18.15) * mm, "end": v(232.8, 24.92) * mm});
            skArc(sketch, "E434.MirrorCS", {"start": v(65.02, -75.64) * mm, "mid": v(73.56, -80.65) * mm, "end": v(83.44, -80.04) * mm});
            skArc(sketch, "E435.MirrorCS", {"start": v(89.9, 4.49) * mm, "mid": v(97.22, 18.15) * mm, "end": v(111.17, 24.92) * mm});
            skLineSegment(sketch, "E436.MirrorCS", {"start": v(164.31, 52.8) * mm, "end": v(164.31, 4.49) * mm});
            skLineSegment(sketch, "E437.MirrorCS", {"start": v(141.97, -50.43) * mm, "end": v(141.97, -21.75) * mm});
            skLineSegment(sketch, "E438.MirrorCS", {"start": v(65, 98.06) * mm, "end": v(83.43, 98.06) * mm});
            skLineSegment(sketch, "E439.MirrorCS", {"start": v(87.35, -50.43) * mm, "end": v(87.35, -21.75) * mm});
            skArc(sketch, "E440.MirrorCS", {"start": v(278.97, 75.52) * mm, "mid": v(270.43, 80.53) * mm, "end": v(260.54, 79.92) * mm});
            skArc(sketch, "E441.MirrorCS", {"start": v(201.04, 9) * mm, "mid": v(208.77, 21.4) * mm, "end": v(221.48, 28.61) * mm});
            skArc(sketch, "E442.MirrorCS", {"start": v(179.66, 52.8) * mm, "mid": v(187.98, 47.77) * mm, "end": v(197.68, 48.2) * mm});
            skLineSegment(sketch, "E443.MirrorCS", {"start": v(243.44, -72.9) * mm, "end": v(243.44, -31.97) * mm});
            skLineSegment(sketch, "E444.MirrorCS", {"start": v(150.85, -25.02) * mm, "end": v(150.85, -42.56) * mm});
            skLineSegment(sketch, "E445.MirrorCS", {"start": v(164.31, 4.49) * mm, "end": v(139.42, 4.49) * mm});
            skLineSegment(sketch, "E446.MirrorCS", {"start": v(278.95, -98.18) * mm, "end": v(278.95, -75.64) * mm});
            skArc(sketch, "E447.MirrorCS", {"start": v(179.68, -75.64) * mm, "mid": v(188.21, -80.65) * mm, "end": v(198.1, -80.04) * mm});
            skArc(sketch, "E448.MirrorCS", {"start": v(278.95, -75.64) * mm, "mid": v(270.41, -80.65) * mm, "end": v(260.53, -80.04) * mm});
            skLineSegment(sketch, "E449.MirrorCS", {"start": v(260.93, -48.31) * mm, "end": v(260.93, -25.02) * mm});
            skLineSegment(sketch, "E450.MirrorCS", {"start": v(179.68, -98.18) * mm, "end": v(198.1, -98.18) * mm});
            skArc(sketch, "E451.MirrorCS", {"start": v(202, -21.75) * mm, "mid": v(207.98, -27.66) * mm, "end": v(215.19, -31.97) * mm});
            skLineSegment(sketch, "E452.MirrorCS", {"start": v(286.64, 105.32) * mm, "end": v(171.99, 105.32) * mm});
            skLineSegment(sketch, "E453.MirrorCS", {"start": v(100.51, 72.78) * mm, "end": v(100.51, 31.85) * mm});
            skLineSegment(sketch, "E454.MirrorCS", {"start": v(179.68, -52.91) * mm, "end": v(179.68, -4.6) * mm});
            skArc(sketch, "E455.MirrorCS", {"start": v(87.33, 21.63) * mm, "mid": v(93.3, 27.54) * mm, "end": v(100.51, 31.85) * mm});
            skArc(sketch, "E456.MirrorCS", {"start": v(257.58, 9) * mm, "mid": v(249.86, 21.4) * mm, "end": v(237.15, 28.61) * mm});
            skCircle(sketch, "E457.MirrorC", {"center": v(229.3, -0.12) * mm, "radius": 19.87 * mm});
            skLineSegment(sketch, "E458.MirrorCS", {"start": v(278.95, -4.6) * mm, "end": v(254.06, -4.6) * mm});
            skArc(sketch, "E459.MirrorCS", {"start": v(141.97, -50.43) * mm, "mid": v(135.25, -60.76) * mm, "end": v(137.32, -72.9) * mm});
            skLineSegment(sketch, "E460.MirrorCS", {"start": v(164.3, -98.18) * mm, "end": v(164.3, -75.64) * mm});
            skLineSegment(sketch, "E461.MirrorCS", {"start": v(92.41, 93.38) * mm, "end": v(106.72, 93.38) * mm});
            skLineSegment(sketch, "E462.MirrorCS", {"start": v(225.84, -98.18) * mm, "end": v(202.88, -98.18) * mm});
            skLineSegment(sketch, "E463.MirrorCS", {"start": v(202, -50.43) * mm, "end": v(202, -21.75) * mm});
            skLineSegment(sketch, "E464.MirrorCS", {"start": v(265.5, -25.02) * mm, "end": v(265.5, -42.56) * mm});
            skLineSegment(sketch, "E465.MirrorCS", {"start": v(57.33, -105.32) * mm, "end": v(171.99, -105.32) * mm});
            skArc(sketch, "E466.MirrorCS", {"start": v(142.93, 9) * mm, "mid": v(135.2, 21.4) * mm, "end": v(122.5, 28.61) * mm});
            skLineSegment(sketch, "E467.MirrorCS", {"start": v(65, 4.49) * mm, "end": v(89.9, 4.49) * mm});
            skLineSegment(sketch, "E468.MirrorCS", {"start": v(278.97, 98.06) * mm, "end": v(278.97, 75.52) * mm});
            skLineSegment(sketch, "E469.MirrorCS", {"start": v(136.9, 93.38) * mm, "end": v(122.6, 93.38) * mm});
            skArc(sketch, "E470.MirrorCS", {"start": v(256.64, 50.3) * mm, "mid": v(249.92, 60.64) * mm, "end": v(252, 72.78) * mm});
            skArc(sketch, "E471.MirrorCS", {"start": v(86.4, -9.11) * mm, "mid": v(94.13, -21.52) * mm, "end": v(106.84, -28.73) * mm});
            skLineSegment(sketch, "E472.MirrorCS", {"start": v(57.33, 105.32) * mm, "end": v(171.99, 105.32) * mm});
            skCircle(sketch, "E473.MirrorC", {"center": v(192.15, -64.18) * mm, "radius": 12.5 * mm});
            skArc(sketch, "E474.MirrorCS", {"start": v(278.97, 52.8) * mm, "mid": v(270.65, 47.77) * mm, "end": v(260.94, 48.2) * mm});
            skArc(sketch, "E475.MirrorCS", {"start": v(65, 75.52) * mm, "mid": v(73.54, 80.53) * mm, "end": v(83.43, 79.92) * mm});
            skLineSegment(sketch, "E476.MirrorCS", {"start": v(136.89, -93.5) * mm, "end": v(122.58, -93.5) * mm});
            skLineSegment(sketch, "E477.MirrorCS", {"start": v(65.02, -4.6) * mm, "end": v(89.91, -4.6) * mm});
            skLineSegment(sketch, "E478.MirrorCS", {"start": v(69.29, 44.03) * mm, "end": v(69.29, 9) * mm});
            skLineSegment(sketch, "E479.MirrorCS", {"start": v(69.29, 9) * mm, "end": v(86.39, 9) * mm});
            skLineSegment(sketch, "E480.MirrorCS", {"start": v(256.64, 50.3) * mm, "end": v(256.64, 21.63) * mm});
            skLineSegment(sketch, "E481.MirrorCS", {"start": v(122.58, -93.5) * mm, "end": v(122.47, -28.73) * mm});
            skLineSegment(sketch, "E482.MirrorCS", {"start": v(221.38, 93.38) * mm, "end": v(221.48, 28.61) * mm});
            skLineSegment(sketch, "E483.MirrorCS", {"start": v(164.3, -52.91) * mm, "end": v(164.3, -4.6) * mm});
            skLineSegment(sketch, "E484.MirrorCS", {"start": v(87.33, 50.3) * mm, "end": v(87.33, 21.63) * mm});
            skLineSegment(sketch, "E485.MirrorCS", {"start": v(225.84, -25.04) * mm, "end": v(225.84, -98.18) * mm});
            skArc(sketch, "E486.MirrorCS", {"start": v(141.98, 21.63) * mm, "mid": v(136.01, 27.54) * mm, "end": v(128.8, 31.85) * mm});
            skLineSegment(sketch, "E487.MirrorCS", {"start": v(118.13, -98.18) * mm, "end": v(141.1, -98.18) * mm});
            skArc(sketch, "E488.MirrorCS", {"start": v(65, 52.8) * mm, "mid": v(73.32, 47.77) * mm, "end": v(83.03, 48.2) * mm});
            skLineSegment(sketch, "E489.MirrorCS", {"start": v(274.67, -44.15) * mm, "end": v(274.67, -9.11) * mm});
            skLineSegment(sketch, "E490.MirrorCS", {"start": v(160.03, 9) * mm, "end": v(142.93, 9) * mm});
            skLineSegment(sketch, "E491.MirrorCS", {"start": v(141.1, 98.06) * mm, "end": v(141.1, 78.94) * mm});
            skLineSegment(sketch, "E492.MirrorCS", {"start": v(179.68, -98.18) * mm, "end": v(179.68, -75.64) * mm});
            skLineSegment(sketch, "E493.MirrorCS", {"start": v(83.04, -48.31) * mm, "end": v(83.04, -25.02) * mm});
            skLineSegment(sketch, "E494.MirrorCS", {"start": v(207.07, 93.38) * mm, "end": v(221.38, 93.38) * mm});
            skCircle(sketch, "E495.MirrorC", {"center": v(114.67, -0.12) * mm, "radius": 19.87 * mm});
            skLineSegment(sketch, "E496.MirrorCS", {"start": v(278.95, -52.91) * mm, "end": v(278.95, -4.6) * mm});
            skArc(sketch, "E497.MirrorCS", {"start": v(201.99, 21.63) * mm, "mid": v(207.96, 27.54) * mm, "end": v(215.17, 31.85) * mm});
            skArc(sketch, "E498.MirrorCS", {"start": v(204.55, 4.49) * mm, "mid": v(211.88, 18.15) * mm, "end": v(225.83, 24.92) * mm});
            skLineSegment(sketch, "E499.MirrorCS", {"start": v(265.52, 24.9) * mm, "end": v(265.52, 42.44) * mm});
            skArc(sketch, "E500.MirrorCS", {"start": v(201.99, 50.3) * mm, "mid": v(208.7, 60.64) * mm, "end": v(206.63, 72.78) * mm});
            skLineSegment(sketch, "E501.MirrorCS", {"start": v(260.54, 98.06) * mm, "end": v(260.54, 79.92) * mm});
            skArc(sketch, "E502.MirrorCS", {"start": v(87.33, 50.3) * mm, "mid": v(94.05, 60.64) * mm, "end": v(91.98, 72.78) * mm});
            skLineSegment(sketch, "E503.MirrorCS", {"start": v(207.08, -93.5) * mm, "end": v(221.4, -93.5) * mm});
            skLineSegment(sketch, "E504.MirrorCS", {"start": v(197.7, -48.31) * mm, "end": v(197.7, -25.02) * mm});
            skLineSegment(sketch, "E505.MirrorCS", {"start": v(118.14, 24.92) * mm, "end": v(118.14, 98.06) * mm});
            skLineSegment(sketch, "E506.MirrorCS", {"start": v(111.18, -98.18) * mm, "end": v(88.22, -98.18) * mm});
            skLineSegment(sketch, "E507.MirrorCS", {"start": v(260.53, -98.18) * mm, "end": v(260.53, -80.04) * mm});
            skLineSegment(sketch, "E508.MirrorCS", {"start": v(78.47, -25.02) * mm, "end": v(78.47, -42.56) * mm});
            skLineSegment(sketch, "E509.MirrorCS", {"start": v(111.17, 24.92) * mm, "end": v(111.17, 98.06) * mm});
            skArc(sketch, "E510.MirrorCS", {"start": v(256.62, -50.43) * mm, "mid": v(249.9, -60.76) * mm, "end": v(251.98, -72.9) * mm});
            skLineSegment(sketch, "E511.MirrorCS", {"start": v(118.14, 98.06) * mm, "end": v(141.1, 98.06) * mm});
            skLineSegment(sketch, "E512.MirrorCS", {"start": v(164.31, 98.06) * mm, "end": v(145.89, 98.06) * mm});
            skLineSegment(sketch, "E513.MirrorCS", {"start": v(65, 52.8) * mm, "end": v(65, 4.49) * mm});
            skArc(sketch, "E514.MirrorCS", {"start": v(254.06, -4.6) * mm, "mid": v(246.73, -18.27) * mm, "end": v(232.79, -25.04) * mm});
            skLineSegment(sketch, "E515.MirrorCS", {"start": v(164.31, 98.06) * mm, "end": v(164.31, 75.52) * mm});
            skLineSegment(sketch, "E516.MirrorCS", {"start": v(278.97, 4.49) * mm, "end": v(254.08, 4.49) * mm});
            skCircle(sketch, "E517.MirrorC", {"center": v(192.13, 64.06) * mm, "radius": 12.5 * mm});
            skCircle(sketch, "E518.MirrorC", {"center": v(266.5, 64.06) * mm, "radius": 12.5 * mm});
            skLineSegment(sketch, "E519.MirrorCS", {"start": v(232.79, -98.18) * mm, "end": v(255.75, -98.18) * mm});
            skLineSegment(sketch, "E520.MirrorCS", {"start": v(193.1, 24.9) * mm, "end": v(193.1, 42.44) * mm});
            skLineSegment(sketch, "E521.MirrorCS", {"start": v(83.43, 98.06) * mm, "end": v(83.43, 79.92) * mm});
            skLineSegment(sketch, "E522.MirrorCS", {"start": v(128.78, -72.9) * mm, "end": v(128.78, -31.97) * mm});
            skLineSegment(sketch, "E523.MirrorCS", {"start": v(232.8, 98.06) * mm, "end": v(255.76, 98.06) * mm});
            skLineSegment(sketch, "E524.MirrorCS", {"start": v(179.66, 4.49) * mm, "end": v(204.55, 4.49) * mm});
            skArc(sketch, "E525.MirrorCS", {"start": v(86.39, 9) * mm, "mid": v(94.11, 21.4) * mm, "end": v(106.82, 28.61) * mm});
            skLineSegment(sketch, "E526.MirrorCS", {"start": v(179.66, 98.06) * mm, "end": v(198.08, 98.06) * mm});
            skArc(sketch, "E527.MirrorCS", {"start": v(142.91, -9.11) * mm, "mid": v(135.19, -21.52) * mm, "end": v(122.47, -28.73) * mm});
            skLineSegment(sketch, "E528.MirrorCS", {"start": v(100.53, -72.9) * mm, "end": v(100.53, -31.97) * mm});
            skLineSegment(sketch, "E529.MirrorCS", {"start": v(122.6, 93.38) * mm, "end": v(122.5, 28.61) * mm});
            skLineSegment(sketch, "E530.MirrorCS", {"start": v(171.99, -105.32) * mm, "end": v(171.99, 105.32) * mm});
            skLineSegment(sketch, "E531.MirrorCS", {"start": v(-321.3, -72.9) * mm, "end": v(-329.84, -72.9) * mm});
            skLineSegment(sketch, "E532.MirrorCS", {"start": v(-366.22, 84.17) * mm, "end": v(-366.22, 93.38) * mm});
            skLineSegment(sketch, "E533.MirrorCS", {"start": v(-198.1, -98.18) * mm, "end": v(-198.1, -80.04) * mm});
            skLineSegment(sketch, "E534.MirrorCS", {"start": v(-202.88, -98.18) * mm, "end": v(-202.88, -79.06) * mm});
            skLineSegment(sketch, "E535.MirrorCS", {"start": v(-207.08, -84.3) * mm, "end": v(-207.08, -93.5) * mm});
            skLineSegment(sketch, "E536.MirrorCS", {"start": v(-202.86, 98.06) * mm, "end": v(-202.86, 78.94) * mm});
            skLineSegment(sketch, "E537.MirrorCS", {"start": v(-366.2, -84.3) * mm, "end": v(-366.2, -93.5) * mm});
            skLineSegment(sketch, "E538.MirrorCS", {"start": v(-251.54, -93.5) * mm, "end": v(-237.23, -93.5) * mm});
            skLineSegment(sketch, "E539.MirrorCS", {"start": v(-241.11, -79.06) * mm, "end": v(-241.11, -84.3) * mm});
            skLineSegment(sketch, "E540.MirrorCS", {"start": v(-294.33, -4.6) * mm, "end": v(-319.22, -4.6) * mm});
            skLineSegment(sketch, "E541.MirrorCS", {"start": v(-197.7, -25.02) * mm, "end": v(-193.12, -25.02) * mm});
            skLineSegment(sketch, "E542.MirrorCS", {"start": v(-206.65, -72.9) * mm, "end": v(-215.19, -72.9) * mm});
            skLineSegment(sketch, "E543.MirrorCS", {"start": v(-355.77, -79.06) * mm, "end": v(-355.77, -84.3) * mm});
            skLineSegment(sketch, "E544.MirrorCS", {"start": v(-321.72, 84.17) * mm, "end": v(-321.72, 93.38) * mm});
            skLineSegment(sketch, "E545.MirrorCS", {"start": v(-375.6, 24.9) * mm, "end": v(-380.18, 24.9) * mm});
            skLineSegment(sketch, "E546.MirrorCS", {"start": v(-375.59, -25.02) * mm, "end": v(-380.16, -25.02) * mm});
            skLineSegment(sketch, "E547.MirrorCS", {"start": v(-355.78, 84.17) * mm, "end": v(-366.22, 84.17) * mm});
            skPoint(sketch, "E548.MirrorP", {"position": v(-229.31, 0) * mm});
            skLineSegment(sketch, "E549.MirrorCS", {"start": v(-370.4, -98.18) * mm, "end": v(-370.4, -79.06) * mm});
            skLineSegment(sketch, "E550.MirrorCS", {"start": v(-251.98, -72.9) * mm, "end": v(-243.44, -72.9) * mm});
            skLineSegment(sketch, "E551.MirrorCS", {"start": v(-370.42, 78.94) * mm, "end": v(-355.78, 78.94) * mm});
            skLineSegment(sketch, "E552.MirrorCS", {"start": v(-317.54, -98.18) * mm, "end": v(-317.54, -79.06) * mm});
            skLineSegment(sketch, "E553.MirrorCS", {"start": v(-198.08, 98.06) * mm, "end": v(-198.08, 79.92) * mm});
            skLineSegment(sketch, "E554.MirrorCS", {"start": v(-207.07, 93.38) * mm, "end": v(-221.38, 93.38) * mm});
            skLineSegment(sketch, "E555.MirrorCS", {"start": v(-355.77, -84.3) * mm, "end": v(-366.2, -84.3) * mm});
            skLineSegment(sketch, "E556.MirrorCS", {"start": v(-217.5, 84.17) * mm, "end": v(-207.07, 84.17) * mm});
            skLineSegment(sketch, "E557.MirrorCS", {"start": v(-251.56, 84.17) * mm, "end": v(-251.56, 93.38) * mm});
            skLineSegment(sketch, "E558.MirrorCS", {"start": v(-317.52, 98.06) * mm, "end": v(-317.52, 78.94) * mm});
            skCircle(sketch, "E559.MirrorC", {"center": v(-192.49, -17.57) * mm, "radius": 4.15 * mm});
            skLineSegment(sketch, "E560.MirrorCS", {"start": v(-298.62, -9.11) * mm, "end": v(-315.72, -9.11) * mm});
            skLineSegment(sketch, "E561.MirrorCS", {"start": v(-217.52, -84.3) * mm, "end": v(-207.08, -84.3) * mm});
            skLineSegment(sketch, "E562.MirrorCS", {"start": v(-370.4, -79.06) * mm, "end": v(-355.77, -79.06) * mm});
            skLineSegment(sketch, "E563.MirrorCS", {"start": v(-370.42, 98.06) * mm, "end": v(-370.42, 78.94) * mm});
            skLineSegment(sketch, "E564.MirrorCS", {"start": v(-217.52, -79.06) * mm, "end": v(-217.52, -84.3) * mm});
            skLineSegment(sketch, "E565.MirrorCS", {"start": v(-241.11, -84.3) * mm, "end": v(-251.54, -84.3) * mm});
            skLineSegment(sketch, "E566.MirrorCS", {"start": v(-255.75, -79.06) * mm, "end": v(-241.11, -79.06) * mm});
            skLineSegment(sketch, "E567.MirrorCS", {"start": v(-332.16, 84.17) * mm, "end": v(-321.72, 84.17) * mm});
            skLineSegment(sketch, "E568.MirrorCS", {"start": v(-241.13, 78.94) * mm, "end": v(-241.13, 84.17) * mm});
            skLineSegment(sketch, "E569.MirrorCS", {"start": v(-183.96, -9.11) * mm, "end": v(-201.06, -9.11) * mm});
            skLineSegment(sketch, "E570.MirrorCS", {"start": v(-225.83, 98.06) * mm, "end": v(-202.86, 98.06) * mm});
            skLineSegment(sketch, "E571.MirrorCS", {"start": v(-241.13, 84.17) * mm, "end": v(-251.56, 84.17) * mm});
            skLineSegment(sketch, "E572.MirrorCS", {"start": v(-321.3, 72.78) * mm, "end": v(-329.83, 72.78) * mm});
            skLineSegment(sketch, "E573.MirrorCS", {"start": v(-207.07, 84.17) * mm, "end": v(-207.07, 93.38) * mm});
            skLineSegment(sketch, "E574.MirrorCS", {"start": v(-251.54, -84.3) * mm, "end": v(-251.54, -93.5) * mm});
            skCircle(sketch, "E575.MirrorC", {"center": v(-307.15, -17.57) * mm, "radius": 4.15 * mm});
            skLineSegment(sketch, "E576.MirrorCS", {"start": v(-312.36, -25.02) * mm, "end": v(-307.78, -25.02) * mm});
            skLineSegment(sketch, "E577.MirrorCS", {"start": v(-202.88, -79.06) * mm, "end": v(-217.52, -79.06) * mm});
            skLineSegment(sketch, "E578.MirrorCS", {"start": v(-312.74, 98.06) * mm, "end": v(-312.74, 79.92) * mm});
            skLineSegment(sketch, "E579.MirrorCS", {"start": v(-317.52, 78.94) * mm, "end": v(-332.16, 78.94) * mm});
            skLineSegment(sketch, "E580.MirrorCS", {"start": v(-206.63, 72.78) * mm, "end": v(-215.17, 72.78) * mm});
            skLineSegment(sketch, "E581.MirrorCS", {"start": v(-255.76, 98.06) * mm, "end": v(-255.76, 78.94) * mm});
            skLineSegment(sketch, "E582.MirrorCS", {"start": v(-332.17, -84.3) * mm, "end": v(-321.74, -84.3) * mm});
            skLineSegment(sketch, "E583.MirrorCS", {"start": v(-274.67, -9.11) * mm, "end": v(-257.57, -9.11) * mm});
            skLineSegment(sketch, "E584.MirrorCS", {"start": v(-317.54, -79.06) * mm, "end": v(-332.17, -79.06) * mm});
            skCircle(sketch, "E585.MirrorC", {"center": v(-343.95, -0.12) * mm, "radius": 19.87 * mm});
            skLineSegment(sketch, "E586.MirrorCS", {"start": v(-366.2, -93.5) * mm, "end": v(-351.9, -93.5) * mm});
            skLineSegment(sketch, "E587.MirrorCS", {"start": v(-260.94, 24.9) * mm, "end": v(-265.52, 24.9) * mm});
            skLineSegment(sketch, "E588.MirrorCS", {"start": v(-278.95, -4.6) * mm, "end": v(-254.06, -4.6) * mm});
            skLineSegment(sketch, "E589.MirrorCS", {"start": v(-332.16, 78.94) * mm, "end": v(-332.16, 84.17) * mm});
            skCircle(sketch, "E590.MirrorC", {"center": v(-380.8, -17.57) * mm, "radius": 4.15 * mm});
            skLineSegment(sketch, "E591.MirrorCS", {"start": v(-294.32, 4.49) * mm, "end": v(-319.2, 4.49) * mm});
            skLineSegment(sketch, "E592.MirrorCS", {"start": v(-321.74, -84.3) * mm, "end": v(-321.74, -93.5) * mm});
            skLineSegment(sketch, "E593.MirrorCS", {"start": v(-355.78, 78.94) * mm, "end": v(-355.78, 84.17) * mm});
            skLineSegment(sketch, "E594.MirrorCS", {"start": v(-197.68, 24.9) * mm, "end": v(-193.1, 24.9) * mm});
            skCircle(sketch, "E595.MirrorC", {"center": v(-229.31, 0) * mm, "radius": 19.87 * mm});
            skLineSegment(sketch, "E596.MirrorCS", {"start": v(-298.6, 9) * mm, "end": v(-315.7, 9) * mm});
            skLineSegment(sketch, "E597.MirrorCS", {"start": v(-183.94, 9) * mm, "end": v(-201.04, 9) * mm});
            skLineSegment(sketch, "E598.MirrorCS", {"start": v(-321.74, -93.5) * mm, "end": v(-336.05, -93.5) * mm});
            skLineSegment(sketch, "E599.MirrorCS", {"start": v(-332.17, -79.06) * mm, "end": v(-332.17, -84.3) * mm});
            skLineSegment(sketch, "E600.MirrorCS", {"start": v(-217.5, 78.94) * mm, "end": v(-217.5, 84.17) * mm});
            skLineSegment(sketch, "E601.MirrorCS", {"start": v(-366.22, 93.38) * mm, "end": v(-351.9, 93.38) * mm});
            skCircle(sketch, "E602.MirrorC", {"center": v(-192.47, 17.45) * mm, "radius": 4.15 * mm});
            skCircle(sketch, "E603.MirrorC", {"center": v(-307.13, 17.45) * mm, "radius": 4.15 * mm});
            skLineSegment(sketch, "E604.MirrorCS", {"start": v(-312.34, 24.9) * mm, "end": v(-307.76, 24.9) * mm});
            skLineSegment(sketch, "E605.MirrorCS", {"start": v(-375.2, 98.06) * mm, "end": v(-375.2, 79.92) * mm});
            skLineSegment(sketch, "E606.MirrorCS", {"start": v(-202.86, 78.94) * mm, "end": v(-217.5, 78.94) * mm});
            skLineSegment(sketch, "E607.MirrorCS", {"start": v(-260.93, -25.02) * mm, "end": v(-265.5, -25.02) * mm});
            skLineSegment(sketch, "E608.MirrorCS", {"start": v(-255.76, 78.94) * mm, "end": v(-241.13, 78.94) * mm});
            skLineSegment(sketch, "E609.MirrorCS", {"start": v(-312.76, -98.18) * mm, "end": v(-312.76, -80.04) * mm});
            skLineSegment(sketch, "E610.MirrorCS", {"start": v(-255.75, -98.18) * mm, "end": v(-255.75, -79.06) * mm});
            skLineSegment(sketch, "E611.MirrorCS", {"start": v(-232.79, -98.18) * mm, "end": v(-255.75, -98.18) * mm});
            skLineSegment(sketch, "E612.MirrorCS", {"start": v(-347.46, 98.06) * mm, "end": v(-370.42, 98.06) * mm});
            skLineSegment(sketch, "E613.MirrorCS", {"start": v(-380.16, -25.02) * mm, "end": v(-380.16, -42.56) * mm});
            skArc(sketch, "E614.MirrorCS", {"start": v(-393.6, -75.64) * mm, "mid": v(-385.07, -80.65) * mm, "end": v(-375.18, -80.04) * mm});
            skArc(sketch, "E615.MirrorCS", {"start": v(-294.33, -75.64) * mm, "mid": v(-302.87, -80.65) * mm, "end": v(-312.76, -80.04) * mm});
            skArc(sketch, "E616.MirrorCS", {"start": v(-265.5, -42.56) * mm, "mid": v(-270.17, -42.86) * mm, "end": v(-274.67, -44.15) * mm});
            skLineSegment(sketch, "E617.MirrorCS", {"start": v(-197.7, -48.31) * mm, "end": v(-197.7, -25.02) * mm});
            skLineSegment(sketch, "E618.MirrorCS", {"start": v(-340.5, -98.18) * mm, "end": v(-317.54, -98.18) * mm});
            skLineSegment(sketch, "E619.MirrorCS", {"start": v(-307.78, -25.02) * mm, "end": v(-307.78, -42.56) * mm});
            skLineSegment(sketch, "E620.MirrorCS", {"start": v(-375.18, -98.18) * mm, "end": v(-375.18, -80.04) * mm});
            skLineSegment(sketch, "E621.MirrorCS", {"start": v(-278.95, -98.18) * mm, "end": v(-278.95, -75.64) * mm});
            skArc(sketch, "E622.MirrorCS", {"start": v(-265.52, 42.44) * mm, "mid": v(-270.19, 42.74) * mm, "end": v(-274.68, 44.03) * mm});
            skArc(sketch, "E623.MirrorCS", {"start": v(-179.66, 75.52) * mm, "mid": v(-188.2, 80.53) * mm, "end": v(-198.08, 79.92) * mm});
            skArc(sketch, "E624.MirrorCS", {"start": v(-256.62, -21.75) * mm, "mid": v(-250.65, -27.66) * mm, "end": v(-243.44, -31.97) * mm});
            skArc(sketch, "E625.MirrorCS", {"start": v(-316.64, 50.3) * mm, "mid": v(-323.36, 60.64) * mm, "end": v(-321.3, 72.78) * mm});
            skLineSegment(sketch, "E626.MirrorCS", {"start": v(-312.34, 48.2) * mm, "end": v(-312.34, 24.9) * mm});
            skLineSegment(sketch, "E627.MirrorCS", {"start": v(-312.36, -48.31) * mm, "end": v(-312.36, -25.02) * mm});
            skLineSegment(sketch, "E628.MirrorCS", {"start": v(-183.96, -44.15) * mm, "end": v(-183.96, -9.11) * mm});
            skLineSegment(sketch, "E629.MirrorCS", {"start": v(-274.68, 9) * mm, "end": v(-257.58, 9) * mm});
            skArc(sketch, "E630.MirrorCS", {"start": v(-371.3, 21.63) * mm, "mid": v(-365.32, 27.54) * mm, "end": v(-358.11, 31.85) * mm});
            skArc(sketch, "E631.MirrorCS", {"start": v(-256.64, 21.63) * mm, "mid": v(-250.67, 27.54) * mm, "end": v(-243.46, 31.85) * mm});
            skLineSegment(sketch, "E632.MirrorCS", {"start": v(-389.32, -9.11) * mm, "end": v(-372.22, -9.11) * mm});
            skArc(sketch, "E633.MirrorCS", {"start": v(-201.06, -9.11) * mm, "mid": v(-208.78, -21.52) * mm, "end": v(-221.5, -28.73) * mm});
            skLineSegment(sketch, "E634.MirrorCS", {"start": v(-294.33, -98.18) * mm, "end": v(-294.33, -75.64) * mm});
            skArc(sketch, "E635.MirrorCS", {"start": v(-294.32, 52.8) * mm, "mid": v(-302.63, 47.77) * mm, "end": v(-312.34, 48.2) * mm});
            skLineSegment(sketch, "E636.MirrorCS", {"start": v(-393.62, 98.06) * mm, "end": v(-375.2, 98.06) * mm});
            skArc(sketch, "E637.MirrorCS", {"start": v(-380.16, -42.56) * mm, "mid": v(-384.83, -42.86) * mm, "end": v(-389.32, -44.15) * mm});
            skArc(sketch, "E638.MirrorCS", {"start": v(-393.62, 75.52) * mm, "mid": v(-385.09, 80.53) * mm, "end": v(-375.2, 79.92) * mm});
            skLineSegment(sketch, "E639.MirrorCS", {"start": v(-252, 72.78) * mm, "end": v(-243.46, 72.78) * mm});
            skArc(sketch, "E640.MirrorCS", {"start": v(-307.78, -42.56) * mm, "mid": v(-303.11, -42.86) * mm, "end": v(-298.62, -44.15) * mm});
            skLineSegment(sketch, "E641.MirrorCS", {"start": v(-366.63, -72.9) * mm, "end": v(-358.1, -72.9) * mm});
            skArc(sketch, "E642.MirrorCS", {"start": v(-201.99, 21.63) * mm, "mid": v(-207.96, 27.54) * mm, "end": v(-215.17, 31.85) * mm});
            skArc(sketch, "E643.MirrorCS", {"start": v(-204.57, -4.6) * mm, "mid": v(-211.9, -18.27) * mm, "end": v(-225.84, -25.04) * mm});
            skCircle(sketch, "E644.MirrorC", {"center": v(-380.81, 17.45) * mm, "radius": 4.15 * mm});
            skArc(sketch, "E645.MirrorCS", {"start": v(-179.68, -52.91) * mm, "mid": v(-188, -47.9) * mm, "end": v(-197.7, -48.31) * mm});
            skLineSegment(sketch, "E646.MirrorCS", {"start": v(-366.65, 72.78) * mm, "end": v(-358.11, 72.78) * mm});
            skArc(sketch, "E647.MirrorCS", {"start": v(-256.64, 50.3) * mm, "mid": v(-249.92, 60.64) * mm, "end": v(-252, 72.78) * mm});
            skArc(sketch, "E648.MirrorCS", {"start": v(-315.72, -9.11) * mm, "mid": v(-323.44, -21.52) * mm, "end": v(-336.15, -28.73) * mm});
            skArc(sketch, "E649.MirrorCS", {"start": v(-316.64, 21.63) * mm, "mid": v(-322.62, 27.54) * mm, "end": v(-329.83, 31.85) * mm});
            skArc(sketch, "E650.MirrorCS", {"start": v(-278.97, 52.8) * mm, "mid": v(-270.65, 47.77) * mm, "end": v(-260.94, 48.2) * mm});
            skArc(sketch, "E651.MirrorCS", {"start": v(-201.99, 50.3) * mm, "mid": v(-208.7, 60.64) * mm, "end": v(-206.63, 72.78) * mm});
            skArc(sketch, "E652.MirrorCS", {"start": v(-372.22, -9.11) * mm, "mid": v(-364.5, -21.52) * mm, "end": v(-351.79, -28.73) * mm});
            skLineSegment(sketch, "E653.MirrorCS", {"start": v(-179.68, -98.18) * mm, "end": v(-179.68, -75.64) * mm});
            skArc(sketch, "E654.MirrorCS", {"start": v(-193.1, 42.44) * mm, "mid": v(-188.44, 42.74) * mm, "end": v(-183.94, 44.03) * mm});
            skArc(sketch, "E655.MirrorCS", {"start": v(-278.95, -52.91) * mm, "mid": v(-270.63, -47.9) * mm, "end": v(-260.93, -48.31) * mm});
            skArc(sketch, "E656.MirrorCS", {"start": v(-294.32, 75.52) * mm, "mid": v(-302.86, 80.53) * mm, "end": v(-312.74, 79.92) * mm});
            skLineSegment(sketch, "E657.MirrorCS", {"start": v(-197.68, 48.2) * mm, "end": v(-197.68, 24.9) * mm});
            skLineSegment(sketch, "E658.MirrorCS", {"start": v(-393.62, 98.06) * mm, "end": v(-393.62, 75.52) * mm});
            skLineSegment(sketch, "E659.MirrorCS", {"start": v(-278.97, 4.49) * mm, "end": v(-254.08, 4.49) * mm});
            skLineSegment(sketch, "E660.MirrorCS", {"start": v(-265.5, -25.02) * mm, "end": v(-265.5, -42.56) * mm});
            skCircle(sketch, "E661.MirrorC", {"center": v(-229.33, -0.12) * mm, "radius": 19.87 * mm});
            skLineSegment(sketch, "E662.MirrorCS", {"start": v(-278.95, -98.18) * mm, "end": v(-260.53, -98.18) * mm});
            skArc(sketch, "E663.MirrorCS", {"start": v(-257.57, -9.11) * mm, "mid": v(-249.84, -21.52) * mm, "end": v(-237.13, -28.73) * mm});
            skLineSegment(sketch, "E664.MirrorCS", {"start": v(-307.76, 24.9) * mm, "end": v(-307.76, 42.44) * mm});
            skLineSegment(sketch, "E665.MirrorCS", {"start": v(-260.94, 48.2) * mm, "end": v(-260.94, 24.9) * mm});
            skLineSegment(sketch, "E666.MirrorCS", {"start": v(-389.34, 9) * mm, "end": v(-372.24, 9) * mm});
            skArc(sketch, "E667.MirrorCS", {"start": v(-380.18, 42.44) * mm, "mid": v(-384.84, 42.74) * mm, "end": v(-389.34, 44.03) * mm});
            skArc(sketch, "E668.MirrorCS", {"start": v(-307.76, 42.44) * mm, "mid": v(-303.1, 42.74) * mm, "end": v(-298.6, 44.03) * mm});
            skArc(sketch, "E669.MirrorCS", {"start": v(-201.04, 9) * mm, "mid": v(-208.77, 21.4) * mm, "end": v(-221.48, 28.61) * mm});
            skArc(sketch, "E670.MirrorCS", {"start": v(-179.66, 52.8) * mm, "mid": v(-187.98, 47.77) * mm, "end": v(-197.68, 48.2) * mm});
            skArc(sketch, "E671.MirrorCS", {"start": v(-202, -21.75) * mm, "mid": v(-207.98, -27.66) * mm, "end": v(-215.19, -31.97) * mm});
            skLineSegment(sketch, "E672.MirrorCS", {"start": v(-294.32, 98.06) * mm, "end": v(-294.32, 75.52) * mm});
            skLineSegment(sketch, "E673.MirrorCS", {"start": v(-316.66, -50.43) * mm, "end": v(-316.66, -21.75) * mm});
            skLineSegment(sketch, "E674.MirrorCS", {"start": v(-260.93, -48.31) * mm, "end": v(-260.93, -25.02) * mm});
            skArc(sketch, "E675.MirrorCS", {"start": v(-278.95, -75.64) * mm, "mid": v(-270.41, -80.65) * mm, "end": v(-260.53, -80.04) * mm});
            skArc(sketch, "E676.MirrorCS", {"start": v(-316.66, -21.75) * mm, "mid": v(-322.63, -27.66) * mm, "end": v(-329.84, -31.97) * mm});
            skLineSegment(sketch, "E677.MirrorCS", {"start": v(-393.6, -98.18) * mm, "end": v(-393.6, -75.64) * mm});
            skLineSegment(sketch, "E678.MirrorCS", {"start": v(-278.97, 98.06) * mm, "end": v(-260.54, 98.06) * mm});
            skLineSegment(sketch, "E679.MirrorCS", {"start": v(-179.66, 98.06) * mm, "end": v(-198.08, 98.06) * mm});
            skLineSegment(sketch, "E680.MirrorCS", {"start": v(-393.6, -98.18) * mm, "end": v(-375.18, -98.18) * mm});
            skArc(sketch, "E681.MirrorCS", {"start": v(-371.28, -21.75) * mm, "mid": v(-365.3, -27.66) * mm, "end": v(-358.1, -31.97) * mm});
            skArc(sketch, "E682.MirrorCS", {"start": v(-204.55, 4.49) * mm, "mid": v(-211.88, 18.15) * mm, "end": v(-225.83, 24.92) * mm});
            skLineSegment(sketch, "E683.MirrorCS", {"start": v(-321.72, 93.38) * mm, "end": v(-336.03, 93.38) * mm});
            skLineSegment(sketch, "E684.MirrorCS", {"start": v(-260.53, -98.18) * mm, "end": v(-260.53, -80.04) * mm});
            skArc(sketch, "E685.MirrorCS", {"start": v(-371.3, 50.3) * mm, "mid": v(-364.58, 60.64) * mm, "end": v(-366.65, 72.78) * mm});
            skArc(sketch, "E686.MirrorCS", {"start": v(-294.33, -52.91) * mm, "mid": v(-302.65, -47.9) * mm, "end": v(-312.36, -48.31) * mm});
            skArc(sketch, "E687.MirrorCS", {"start": v(-372.24, 9) * mm, "mid": v(-364.52, 21.4) * mm, "end": v(-351.8, 28.61) * mm});
            skLineSegment(sketch, "E688.MirrorCS", {"start": v(-393.62, 4.49) * mm, "end": v(-368.73, 4.49) * mm});
            skLineSegment(sketch, "E689.MirrorCS", {"start": v(-316.64, 50.3) * mm, "end": v(-316.64, 21.63) * mm});
            skArc(sketch, "E690.MirrorCS", {"start": v(-393.6, -52.91) * mm, "mid": v(-385.3, -47.9) * mm, "end": v(-375.59, -48.31) * mm});
            skLineSegment(sketch, "E691.MirrorCS", {"start": v(-179.68, -98.18) * mm, "end": v(-198.1, -98.18) * mm});
            skLineSegment(sketch, "E692.MirrorCS", {"start": v(-179.66, 98.06) * mm, "end": v(-179.66, 75.52) * mm});
            skArc(sketch, "E693.MirrorCS", {"start": v(-319.22, -4.6) * mm, "mid": v(-326.55, -18.27) * mm, "end": v(-340.5, -25.04) * mm});
            skArc(sketch, "E694.MirrorCS", {"start": v(-393.62, 52.8) * mm, "mid": v(-385.3, 47.77) * mm, "end": v(-375.6, 48.2) * mm});
            skLineSegment(sketch, "E695.MirrorCS", {"start": v(-193.1, 24.9) * mm, "end": v(-193.1, 42.44) * mm});
            skArc(sketch, "E696.MirrorCS", {"start": v(-315.7, 9) * mm, "mid": v(-323.43, 21.4) * mm, "end": v(-336.14, 28.61) * mm});
            skCircle(sketch, "E697.MirrorC", {"center": v(-266.14, -17.57) * mm, "radius": 4.15 * mm});
            skLineSegment(sketch, "E698.MirrorCS", {"start": v(-371.28, -50.43) * mm, "end": v(-371.28, -21.75) * mm});
            skLineSegment(sketch, "E699.MirrorCS", {"start": v(-225.84, -98.18) * mm, "end": v(-202.88, -98.18) * mm});
            skArc(sketch, "E700.MirrorCS", {"start": v(-368.73, 4.49) * mm, "mid": v(-361.4, 18.15) * mm, "end": v(-347.46, 24.92) * mm});
            skLineSegment(sketch, "E701.MirrorCS", {"start": v(-375.6, 48.2) * mm, "end": v(-375.6, 24.9) * mm});
            skLineSegment(sketch, "E702.MirrorCS", {"start": v(-256.64, 50.3) * mm, "end": v(-256.64, 21.63) * mm});
            skLineSegment(sketch, "E703.MirrorCS", {"start": v(-260.54, 98.06) * mm, "end": v(-260.54, 79.92) * mm});
            skArc(sketch, "E704.MirrorCS", {"start": v(-254.08, 4.49) * mm, "mid": v(-246.75, 18.15) * mm, "end": v(-232.8, 24.92) * mm});
            skLineSegment(sketch, "E705.MirrorCS", {"start": v(-375.59, -48.31) * mm, "end": v(-375.59, -25.02) * mm});
            skLineSegment(sketch, "E706.MirrorCS", {"start": v(-251.56, 93.38) * mm, "end": v(-237.25, 93.38) * mm});
            skArc(sketch, "E707.MirrorCS", {"start": v(-278.97, 75.52) * mm, "mid": v(-270.43, 80.53) * mm, "end": v(-260.54, 79.92) * mm});
            skLineSegment(sketch, "E708.MirrorCS", {"start": v(-371.3, 50.3) * mm, "end": v(-371.3, 21.63) * mm});
            skArc(sketch, "E709.MirrorCS", {"start": v(-319.2, 4.49) * mm, "mid": v(-326.54, 18.15) * mm, "end": v(-340.48, 24.92) * mm});
            skLineSegment(sketch, "E710.MirrorCS", {"start": v(-265.52, 24.9) * mm, "end": v(-265.52, 42.44) * mm});
            skLineSegment(sketch, "E711.MirrorCS", {"start": v(-183.94, 44.03) * mm, "end": v(-183.94, 9) * mm});
            skLineSegment(sketch, "E712.MirrorCS", {"start": v(-179.66, 4.49) * mm, "end": v(-204.55, 4.49) * mm});
            skLineSegment(sketch, "E713.MirrorCS", {"start": v(-294.32, 98.06) * mm, "end": v(-312.74, 98.06) * mm});
            skArc(sketch, "E714.MirrorCS", {"start": v(-193.12, -42.56) * mm, "mid": v(-188.46, -42.86) * mm, "end": v(-183.96, -44.15) * mm});
            skLineSegment(sketch, "E715.MirrorCS", {"start": v(-380.18, 24.9) * mm, "end": v(-380.18, 42.44) * mm});
            skArc(sketch, "E716.MirrorCS", {"start": v(-179.68, -75.64) * mm, "mid": v(-188.21, -80.65) * mm, "end": v(-198.1, -80.04) * mm});
            skLineSegment(sketch, "E717.MirrorCS", {"start": v(-256.62, -50.43) * mm, "end": v(-256.62, -21.75) * mm});
            skLineSegment(sketch, "E718.MirrorCS", {"start": v(-193.12, -25.02) * mm, "end": v(-193.12, -42.56) * mm});
            skLineSegment(sketch, "E719.MirrorCS", {"start": v(-340.48, 98.06) * mm, "end": v(-317.52, 98.06) * mm});
            skLineSegment(sketch, "E720.MirrorCS", {"start": v(-179.68, -4.6) * mm, "end": v(-204.57, -4.6) * mm});
            skLineSegment(sketch, "E721.MirrorCS", {"start": v(-347.44, -98.18) * mm, "end": v(-370.4, -98.18) * mm});
            skLineSegment(sketch, "E722.MirrorCS", {"start": v(-207.08, -93.5) * mm, "end": v(-221.4, -93.5) * mm});
            skLineSegment(sketch, "E723.MirrorCS", {"start": v(-232.8, 98.06) * mm, "end": v(-255.76, 98.06) * mm});
            skLineSegment(sketch, "E724.MirrorCS", {"start": v(-294.33, -98.18) * mm, "end": v(-312.76, -98.18) * mm});
            skCircle(sketch, "E725.MirrorC", {"center": v(-266.15, 17.45) * mm, "radius": 4.15 * mm});
            skLineSegment(sketch, "E726.MirrorCS", {"start": v(-278.97, 98.06) * mm, "end": v(-278.97, 75.52) * mm});
            skArc(sketch, "E727.MirrorCS", {"start": v(-368.72, -4.6) * mm, "mid": v(-361.39, -18.27) * mm, "end": v(-347.44, -25.04) * mm});
            skArc(sketch, "E728.MirrorCS", {"start": v(-254.06, -4.6) * mm, "mid": v(-246.73, -18.27) * mm, "end": v(-232.79, -25.04) * mm});
            skArc(sketch, "E729.MirrorCS", {"start": v(-257.58, 9) * mm, "mid": v(-249.86, 21.4) * mm, "end": v(-237.15, 28.61) * mm});
            skCircle(sketch, "E730.MirrorC", {"center": v(-343.97, 0) * mm, "radius": 19.87 * mm});
            skLineSegment(sketch, "E731.MirrorCS", {"start": v(-393.6, -4.6) * mm, "end": v(-368.72, -4.6) * mm});
            skCircle(sketch, "E732.MirrorC", {"center": v(-343.99, -0.12) * mm, "radius": 19.87 * mm});
            skCircle(sketch, "E733.MirrorC", {"center": v(-229.3, -0.12) * mm, "radius": 19.87 * mm});
            skLineSegment(sketch, "E734.MirrorCS", {"start": v(-298.6, 44.03) * mm, "end": v(-298.6, 9) * mm});
            skLineSegment(sketch, "E735.MirrorCS", {"start": v(-274.67, -44.15) * mm, "end": v(-274.67, -9.11) * mm});
            skLineSegment(sketch, "E736.MirrorCS", {"start": v(-389.32, -44.15) * mm, "end": v(-389.32, -9.11) * mm});
            skLineSegment(sketch, "E737.MirrorCS", {"start": v(-298.62, -44.15) * mm, "end": v(-298.62, -9.11) * mm});
            skLineSegment(sketch, "E738.MirrorCS", {"start": v(-340.48, 24.92) * mm, "end": v(-340.48, 98.06) * mm});
            skCircle(sketch, "E739.MirrorC", {"center": v(-381.13, -64.18) * mm, "radius": 12.5 * mm});
            skLineSegment(sketch, "E740.MirrorCS", {"start": v(-221.4, -93.5) * mm, "end": v(-221.5, -28.73) * mm});
            skLineSegment(sketch, "E741.MirrorCS", {"start": v(-274.68, 44.03) * mm, "end": v(-274.68, 9) * mm});
            skCircle(sketch, "E742.MirrorC", {"center": v(-192.15, -64.18) * mm, "radius": 12.5 * mm});
            skLineSegment(sketch, "E743.MirrorCS", {"start": v(-232.79, -25.04) * mm, "end": v(-232.79, -98.18) * mm});
            skCircle(sketch, "E744.MirrorC", {"center": v(-192.13, 64.06) * mm, "radius": 12.5 * mm});
            skLineSegment(sketch, "E745.MirrorCS", {"start": v(-179.66, 52.8) * mm, "end": v(-179.66, 4.49) * mm});
            skLineSegment(sketch, "E746.MirrorCS", {"start": v(-215.19, -72.9) * mm, "end": v(-215.19, -31.97) * mm});
            skLineSegment(sketch, "E747.MirrorCS", {"start": v(-329.84, -72.9) * mm, "end": v(-329.84, -31.97) * mm});
            skLineSegment(sketch, "E748.MirrorCS", {"start": v(-202, -50.43) * mm, "end": v(-202, -21.75) * mm});
            skLineSegment(sketch, "E749.MirrorCS", {"start": v(-278.97, 52.8) * mm, "end": v(-278.97, 4.49) * mm});
            skLineSegment(sketch, "E750.MirrorCS", {"start": v(-351.9, -93.5) * mm, "end": v(-351.79, -28.73) * mm});
            skLineSegment(sketch, "E751.MirrorCS", {"start": v(-171.99, 105.32) * mm, "end": v(-286.64, 105.32) * mm});
            skLineSegment(sketch, "E752.MirrorCS", {"start": v(-278.95, -52.91) * mm, "end": v(-278.95, -4.6) * mm});
            skLineSegment(sketch, "E753.MirrorCS", {"start": v(-351.9, 93.38) * mm, "end": v(-351.8, 28.61) * mm});
            skLineSegment(sketch, "E754.MirrorCS", {"start": v(-232.8, 24.92) * mm, "end": v(-232.8, 98.06) * mm});
            skLineSegment(sketch, "E755.MirrorCS", {"start": v(-401.3, 105.32) * mm, "end": v(-286.64, 105.32) * mm});
            skLineSegment(sketch, "E756.MirrorCS", {"start": v(-401.3, -105.32) * mm, "end": v(-286.64, -105.32) * mm});
            skLineSegment(sketch, "E757.MirrorCS", {"start": v(-179.68, -52.91) * mm, "end": v(-179.68, -4.6) * mm});
            skLineSegment(sketch, "E758.MirrorCS", {"start": v(-393.62, 52.8) * mm, "end": v(-393.62, 4.49) * mm});
            skLineSegment(sketch, "E759.MirrorCS", {"start": v(-225.83, 24.92) * mm, "end": v(-225.83, 98.06) * mm});
            skLineSegment(sketch, "E760.MirrorCS", {"start": v(-329.83, 72.78) * mm, "end": v(-329.83, 31.85) * mm});
            skLineSegment(sketch, "E761.MirrorCS", {"start": v(-358.1, -72.9) * mm, "end": v(-358.1, -31.97) * mm});
            skLineSegment(sketch, "E762.MirrorCS", {"start": v(-358.11, 72.78) * mm, "end": v(-358.11, 31.85) * mm});
            skLineSegment(sketch, "E763.MirrorCS", {"start": v(-294.33, -52.91) * mm, "end": v(-294.33, -4.6) * mm});
            skCircle(sketch, "E764.MirrorC", {"center": v(-381.15, 64.06) * mm, "radius": 12.5 * mm});
            skCircle(sketch, "E765.MirrorC", {"center": v(-306.8, -64.18) * mm, "radius": 12.5 * mm});
            skLineSegment(sketch, "E766.MirrorCS", {"start": v(-294.32, 52.8) * mm, "end": v(-294.32, 4.49) * mm});
            skArc(sketch, "E767.MirrorCS", {"start": v(-316.66, -50.43) * mm, "mid": v(-323.38, -60.76) * mm, "end": v(-321.3, -72.9) * mm});
            skArc(sketch, "E768.MirrorCS", {"start": v(-202, -50.43) * mm, "mid": v(-208.72, -60.76) * mm, "end": v(-206.65, -72.9) * mm});
            skLineSegment(sketch, "E769.MirrorCS", {"start": v(-347.44, -25.04) * mm, "end": v(-347.44, -98.18) * mm});
            skCircle(sketch, "E770.MirrorC", {"center": v(-306.79, 64.06) * mm, "radius": 12.5 * mm});
            skLineSegment(sketch, "E771.MirrorCS", {"start": v(-347.46, 24.92) * mm, "end": v(-347.46, 98.06) * mm});
            skCircle(sketch, "E772.MirrorC", {"center": v(-266.5, 64.06) * mm, "radius": 12.5 * mm});
            skLineSegment(sketch, "E773.MirrorCS", {"start": v(-237.23, -93.5) * mm, "end": v(-237.13, -28.73) * mm});
            skLineSegment(sketch, "E774.MirrorCS", {"start": v(-201.99, 50.3) * mm, "end": v(-201.99, 21.63) * mm});
            skLineSegment(sketch, "E775.MirrorCS", {"start": v(-243.46, 72.78) * mm, "end": v(-243.46, 31.85) * mm});
            skLineSegment(sketch, "E776.MirrorCS", {"start": v(-393.6, -52.91) * mm, "end": v(-393.6, -4.6) * mm});
            skLineSegment(sketch, "E777.MirrorCS", {"start": v(-336.03, 93.38) * mm, "end": v(-336.14, 28.61) * mm});
            skLineSegment(sketch, "E778.MirrorCS", {"start": v(-221.38, 93.38) * mm, "end": v(-221.48, 28.61) * mm});
            skArc(sketch, "E779.MirrorCS", {"start": v(-256.62, -50.43) * mm, "mid": v(-249.9, -60.76) * mm, "end": v(-251.98, -72.9) * mm});
            skArc(sketch, "E780.MirrorCS", {"start": v(-371.28, -50.43) * mm, "mid": v(-364.56, -60.76) * mm, "end": v(-366.63, -72.9) * mm});
            skLineSegment(sketch, "E781.MirrorCS", {"start": v(-336.05, -93.5) * mm, "end": v(-336.15, -28.73) * mm});
            skCircle(sketch, "E782.MirrorC", {"center": v(-266.48, -64.18) * mm, "radius": 12.5 * mm});
            skLineSegment(sketch, "E783.MirrorCS", {"start": v(-237.25, 93.38) * mm, "end": v(-237.15, 28.61) * mm});
            skLineSegment(sketch, "E784.MirrorCS", {"start": v(-225.84, -25.04) * mm, "end": v(-225.84, -98.18) * mm});
            skLineSegment(sketch, "E785.MirrorCS", {"start": v(-215.17, 72.78) * mm, "end": v(-215.17, 31.85) * mm});
            skLineSegment(sketch, "E786.MirrorCS", {"start": v(-243.44, -72.9) * mm, "end": v(-243.44, -31.97) * mm});
            skLineSegment(sketch, "E787.MirrorCS", {"start": v(-389.34, 44.03) * mm, "end": v(-389.34, 9) * mm});
            skLineSegment(sketch, "E788.MirrorCS", {"start": v(-171.99, -105.32) * mm, "end": v(-286.64, -105.32) * mm});
            skLineSegment(sketch, "E789.MirrorCS", {"start": v(-401.3, -105.32) * mm, "end": v(-401.3, 105.32) * mm});
            skLineSegment(sketch, "E790.MirrorCS", {"start": v(-340.5, -25.04) * mm, "end": v(-340.5, -98.18) * mm});
            skLineSegment(sketch, "E791.MirrorCS", {"start": v(-286.64, -105.32) * mm, "end": v(-286.64, 105.32) * mm});
            skSolve(sketch);
        }
        {
            var Q0;
            Q0=makeQuery(id+"F0.imprint","IMPRINT",FACE,{"disambiguationData":[TD([[makeQuery(id+"F0.imprint","IMPRINT",EDGE,{"derivedFrom":sQuery(id+"F0.wireOp",EDGE,"E0.right")}),1.0]])]});
            var Q1;
            Q1=makeQuery(id+"F0.imprint","IMPRINT",FACE,{"disambiguationData":[TD([[makeQuery(id+"F0.imprint","IMPRINT",EDGE,{"derivedFrom":sQuery(id+"F0.wireOp",EDGE,"E312.MirrorCS")}),1.0]])]});
            var Q2;
            Q2=makeQuery(id+"F0.imprint","IMPRINT",FACE,{"disambiguationData":[TD([[makeQuery(id+"F0.imprint","IMPRINT",EDGE,{"derivedFrom":sQuery(id+"F0.wireOp",EDGE,"E335.MirrorCS")}),1.0]])]});
            var Q3;
            Q3=makeQuery(id+"F0.imprint","IMPRINT",FACE,{"disambiguationData":[TD([[makeQuery(id+"F0.imprint","IMPRINT",EDGE,{"derivedFrom":sQuery(id+"F0.wireOp",EDGE,"E0.right")}),-1.0]])]});
            var Q4;
            Q4=makeQuery(id+"F0.imprint","IMPRINT",FACE,{"disambiguationData":[TD([[makeQuery(id+"F0.imprint","IMPRINT",EDGE,{"derivedFrom":sQuery(id+"F0.wireOp",EDGE,"E531.MirrorCS")}),1.0]])]});
            var Q5;
            Q5=makeQuery(id+"F0.imprint","IMPRINT",FACE,{"disambiguationData":[TD([[makeQuery(id+"F0.imprint","IMPRINT",EDGE,{"derivedFrom":sQuery(id+"F0.wireOp",EDGE,"E535.MirrorCS")}),-1.0]])]});
            extrude(context, id + "F1", {"entities" : qUnion([Q0, Q1, Q2, Q3, Q4, Q5]), "depth" : 1.5 * mm, "offsetDistance" : 25 * mm});
        }
    });
